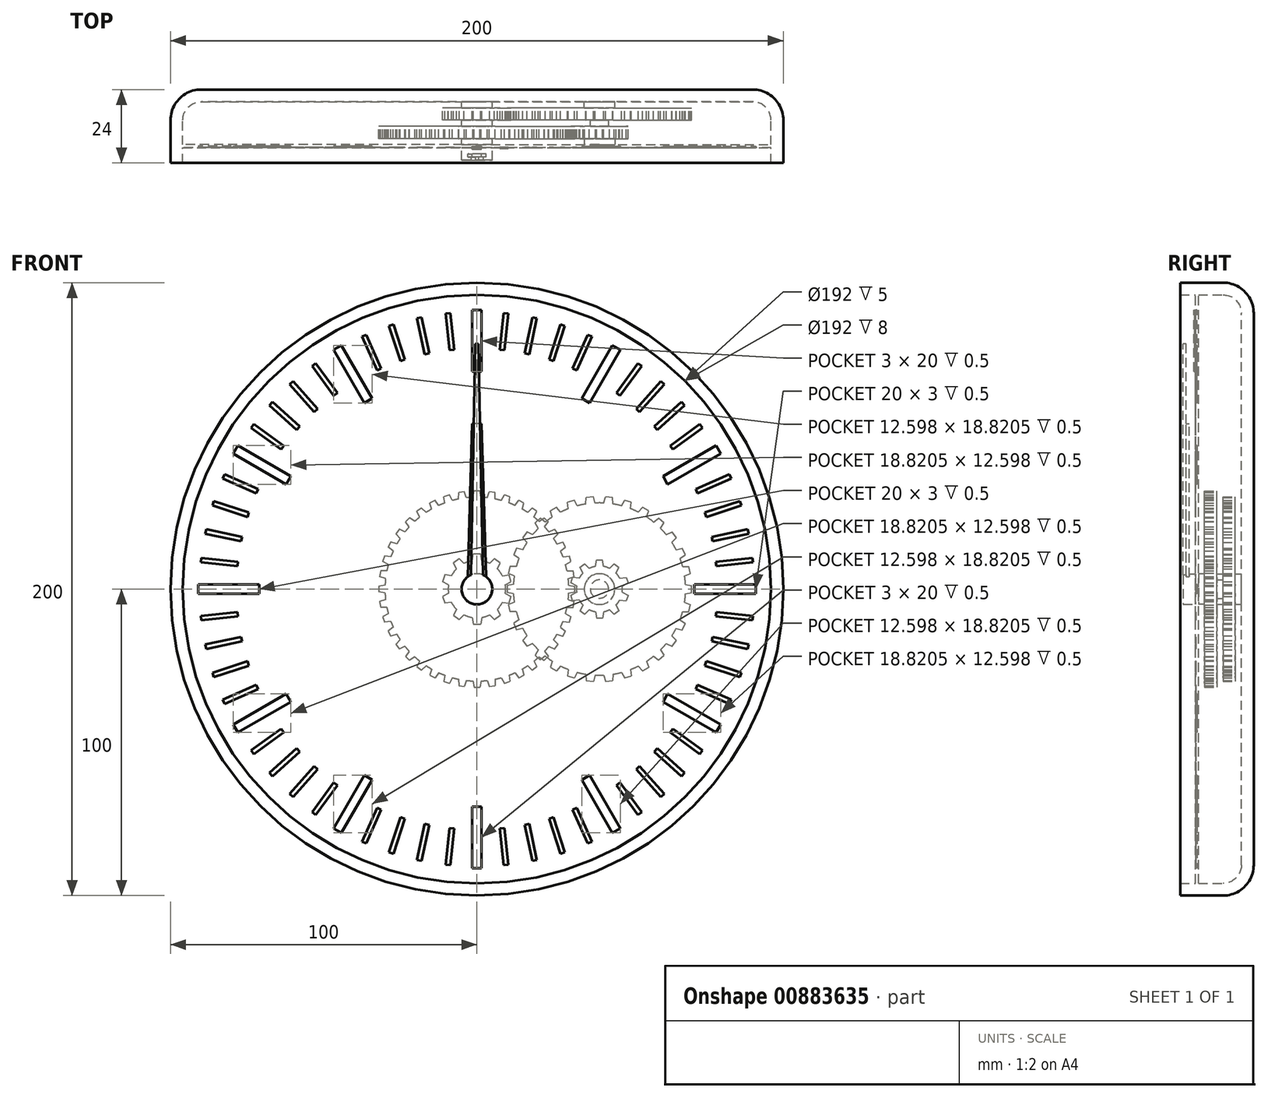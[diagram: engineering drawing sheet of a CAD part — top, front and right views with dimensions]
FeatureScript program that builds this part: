
annotation { "Feature Type Name" : "Feature", "Feature Type Description" : "" }
export const myFeature = defineFeature(function(context is Context, id is Id, definition is map)
    precondition{}
    {
        {
            var Q0;
            Q0=qCreatedBy(makeId("Front.planeOp"),FACE);
            var sketch = newSketch(context, id + "F0", { "sketchPlane" : qUnion([Q0])});
            skCircle(sketch, "E0", {"center": v(0, 0) * mm, "radius": 100 * mm});
            skSolve(sketch);
        }
        {
            var Q0;
            Q0 = qSketchRegion(id + "F0", true);
            extrude(context, id + "F1", {"entities" : qUnion([Q0]), "depth" : 24 * mm, "offsetDistance" : 25 * mm});
        }
        {
            var Q0;
            Q0=makeQuery(id+"F1.opExtrude","CAP_EDGE",EDGE,{"disambiguationData":[OSD([sQuery(id+"F0.wireOp",EDGE,"E0")])],"isStart":true});
            fillet(context, id + "F2", {"entities" : qUnion([Q0]), "radius" : 10 * mm, "tangentPropagation" : true, "allowEdgeOverflow" : false});
        }
        {
            var Q0;
            Q0=makeQuery(id+"F1.opExtrude","CAP_FACE",FACE,{"disambiguationData":[OSD([sQuery(id+"F0.wireOp",EDGE,"E0")])],"isStart":false});
            shell(context, id + "F3", {"entities" : qUnion([Q0]), "thickness" : 4 * mm});
        }
        {
            var Q0;
            {var subQ0=sQuery(id+"F0.wireOp",EDGE,"E0");Q0=makeQuery(id+"F3.opShell","OFFSET_FACE",FACE,{"disambiguationData":[OSD([subQ0]),TDD([makeQuery(id+"F1.opExtrude","CAP_FACE",FACE,{"disambiguationData":[OSD([subQ0])],"isStart":true})])]});}
            var sketch = newSketch(context, id + "F4", { "sketchPlane" : qUnion([Q0])});
            skCircle(sketch, "E1", {"center": v(40, 0) * mm, "radius": 3 * mm});
            skCircle(sketch, "E2", {"center": v(40, 0) * mm, "radius": 5 * mm});
            skCircle(sketch, "E3", {"center": v(0, 0) * mm, "radius": 3 * mm});
            skCircle(sketch, "E4", {"center": v(0, 0) * mm, "radius": 5 * mm});
            skSolve(sketch);
        }
        {
            var Q0;
            Q0 = qSketchRegion(id + "F4", true);
            extrude(context, id + "F5", {"entities" : qUnion([Q0]), "operationType" : NewBodyOperationType.ADD, "depth" : 2 * mm, "offsetDistance" : 25 * mm});
        }
        {
            var Q0;
            {var subQ0=sQuery(id+"F0.wireOp",EDGE,"E0");Q0=makeQuery(id+"F5.boolean.opBoolean","SPLIT",FACE,{"disambiguationData":[TD([makeQuery(id+"F5.opExtrude","SWEPT_FACE",FACE,{"disambiguationData":[OSD([sQuery(id+"F4.wireOp",EDGE,"E3")])]})])],"derivedFrom":makeQuery(id+"F3.opShell","OFFSET_FACE",FACE,{"disambiguationData":[OSD([subQ0]),TDD([makeQuery(id+"F1.opExtrude","CAP_FACE",FACE,{"disambiguationData":[OSD([subQ0])],"isStart":true})])]})});}
            extrude(context, id + "F6", {"entities" : qUnion([Q0]), "depth" : 19 * mm, "offsetDistance" : 25 * mm});
        }
        {
            var Q0;
            {var subQ0=sQuery(id+"F0.wireOp",EDGE,"E0");Q0=makeQuery(id+"F5.boolean.opBoolean","SPLIT",FACE,{"disambiguationData":[TD([makeQuery(id+"F5.opExtrude","SWEPT_FACE",FACE,{"disambiguationData":[OSD([sQuery(id+"F4.wireOp",EDGE,"E1")])]})])],"derivedFrom":makeQuery(id+"F3.opShell","OFFSET_FACE",FACE,{"disambiguationData":[OSD([subQ0]),TDD([makeQuery(id+"F1.opExtrude","CAP_FACE",FACE,{"disambiguationData":[OSD([subQ0])],"isStart":true})])]})});}
            extrude(context, id + "F7", {"entities" : qUnion([Q0]), "depth" : 8 * mm, "offsetDistance" : 25 * mm});
        }
        {
            var Q0;
            Q0=makeQuery(id+"F5.opExtrude","CAP_FACE",FACE,{"disambiguationData":[OSD([sQuery(id+"F4.wireOp",EDGE,"E3"),sQuery(id+"F4.wireOp",EDGE,"E4")])],"isStart":false});
            var sketch = newSketch(context, id + "F8", { "sketchPlane" : qUnion([Q0])});
            skCircle(sketch, "E5", {"center": v(0, 0) * mm, "radius": 9.38 * mm});
            skLineSegment(sketch, "E6", {"start": v(1.55, 9.25) * mm, "end": v(1.18, 11.38) * mm});
            skLineSegment(sketch, "E7", {"start": v(1.18, 11.38) * mm, "end": v(0, 11.38) * mm});
            skLineSegment(sketch, "E8.MirrorCS", {"start": v(-1.18, 11.38) * mm, "end": v(0, 11.38) * mm});
            skLineSegment(sketch, "E9.MirrorCS", {"start": v(-1.55, 9.25) * mm, "end": v(-1.18, 11.38) * mm});
            skLineSegment(sketch, "E10.1.0", {"start": v(-6.7, 6.57) * mm, "end": v(-7.64, 8.51) * mm});
            skLineSegment(sketch, "E10.1.1", {"start": v(-7.64, 8.51) * mm, "end": v(-6.69, 9.2) * mm});
            skLineSegment(sketch, "E10.1.2", {"start": v(-5.73, 9.9) * mm, "end": v(-6.69, 9.2) * mm});
            skLineSegment(sketch, "E10.1.3", {"start": v(-4.18, 8.4) * mm, "end": v(-5.73, 9.9) * mm});
            skLineSegment(sketch, "E10.2.0", {"start": v(-9.27, 1.38) * mm, "end": v(-11.18, 2.4) * mm});
            skLineSegment(sketch, "E10.2.1", {"start": v(-11.18, 2.4) * mm, "end": v(-10.82, 3.52) * mm});
            skLineSegment(sketch, "E10.2.2", {"start": v(-10.45, 4.64) * mm, "end": v(-10.82, 3.52) * mm});
            skLineSegment(sketch, "E10.2.3", {"start": v(-8.31, 4.33) * mm, "end": v(-10.45, 4.64) * mm});
            skLineSegment(sketch, "E11.1.3.0", {"start": v(-8.31, -4.33) * mm, "end": v(-10.45, -4.64) * mm});
            skLineSegment(sketch, "E11.3.3.0", {"start": v(-10.45, -4.64) * mm, "end": v(-10.82, -3.52) * mm});
            skLineSegment(sketch, "E11.6.3.0", {"start": v(-11.18, -2.4) * mm, "end": v(-10.82, -3.52) * mm});
            skLineSegment(sketch, "E11.9.3.0", {"start": v(-9.27, -1.38) * mm, "end": v(-11.18, -2.4) * mm});
            skLineSegment(sketch, "E11.1.4.0", {"start": v(-4.18, -8.4) * mm, "end": v(-5.73, -9.9) * mm});
            skLineSegment(sketch, "E11.3.4.0", {"start": v(-5.73, -9.9) * mm, "end": v(-6.69, -9.2) * mm});
            skLineSegment(sketch, "E11.6.4.0", {"start": v(-7.64, -8.51) * mm, "end": v(-6.69, -9.2) * mm});
            skLineSegment(sketch, "E11.9.4.0", {"start": v(-6.7, -6.57) * mm, "end": v(-7.64, -8.51) * mm});
            skLineSegment(sketch, "E11.1.5.0", {"start": v(1.55, -9.25) * mm, "end": v(1.18, -11.38) * mm});
            skLineSegment(sketch, "E11.3.5.0", {"start": v(1.18, -11.38) * mm, "end": v(0, -11.38) * mm});
            skLineSegment(sketch, "E11.6.5.0", {"start": v(-1.18, -11.38) * mm, "end": v(0, -11.38) * mm});
            skLineSegment(sketch, "E11.9.5.0", {"start": v(-1.55, -9.25) * mm, "end": v(-1.18, -11.38) * mm});
            skLineSegment(sketch, "E11.1.6.0", {"start": v(6.7, -6.57) * mm, "end": v(7.64, -8.51) * mm});
            skLineSegment(sketch, "E11.3.6.0", {"start": v(7.64, -8.51) * mm, "end": v(6.69, -9.2) * mm});
            skLineSegment(sketch, "E11.6.6.0", {"start": v(5.73, -9.9) * mm, "end": v(6.69, -9.2) * mm});
            skLineSegment(sketch, "E11.9.6.0", {"start": v(4.18, -8.4) * mm, "end": v(5.73, -9.9) * mm});
            skLineSegment(sketch, "E11.1.7.0", {"start": v(9.27, -1.38) * mm, "end": v(11.18, -2.4) * mm});
            skLineSegment(sketch, "E11.3.7.0", {"start": v(11.18, -2.4) * mm, "end": v(10.82, -3.52) * mm});
            skLineSegment(sketch, "E11.6.7.0", {"start": v(10.45, -4.64) * mm, "end": v(10.82, -3.52) * mm});
            skLineSegment(sketch, "E11.9.7.0", {"start": v(8.31, -4.33) * mm, "end": v(10.45, -4.64) * mm});
            skLineSegment(sketch, "E11.1.8.0", {"start": v(8.31, 4.33) * mm, "end": v(10.45, 4.64) * mm});
            skLineSegment(sketch, "E11.3.8.0", {"start": v(10.45, 4.64) * mm, "end": v(10.82, 3.52) * mm});
            skLineSegment(sketch, "E11.6.8.0", {"start": v(11.18, 2.4) * mm, "end": v(10.82, 3.52) * mm});
            skLineSegment(sketch, "E11.9.8.0", {"start": v(9.27, 1.38) * mm, "end": v(11.18, 2.4) * mm});
            skLineSegment(sketch, "E11.1.9.0", {"start": v(4.18, 8.4) * mm, "end": v(5.73, 9.9) * mm});
            skLineSegment(sketch, "E11.3.9.0", {"start": v(5.73, 9.9) * mm, "end": v(6.69, 9.2) * mm});
            skLineSegment(sketch, "E11.6.9.0", {"start": v(7.64, 8.51) * mm, "end": v(6.69, 9.2) * mm});
            skLineSegment(sketch, "E11.9.9.0", {"start": v(6.7, 6.57) * mm, "end": v(7.64, 8.51) * mm});
            skSolve(sketch);
        }
        {
            var Q0;
            Q0 = qSketchRegion(id + "F8", true);
            extrude(context, id + "F9", {"entities" : qUnion([Q0]), "operationType" : NewBodyOperationType.ADD, "depth" : 4 * mm, "offsetDistance" : 25 * mm});
        }
        {
            var Q0;
            Q0=makeQuery(id+"F5.opExtrude","CAP_FACE",FACE,{"disambiguationData":[OSD([sQuery(id+"F4.wireOp",EDGE,"E1"),sQuery(id+"F4.wireOp",EDGE,"E2")])],"isStart":false});
            var sketch = newSketch(context, id + "F10", { "sketchPlane" : qUnion([Q0])});
            skCircle(sketch, "E12", {"center": v(40, 0) * mm, "radius": 28.12 * mm});
            skLineSegment(sketch, "E13", {"start": v(11.92, 1.54) * mm, "end": v(9.88, 1.18) * mm});
            skLineSegment(sketch, "E14", {"start": v(9.88, 1.18) * mm, "end": v(9.88, 0) * mm});
            skLineSegment(sketch, "E15.MirrorCS", {"start": v(11.92, -1.54) * mm, "end": v(9.88, -1.18) * mm});
            skLineSegment(sketch, "E16.MirrorCS", {"start": v(9.88, -1.18) * mm, "end": v(9.88, 0) * mm});
            skLineSegment(sketch, "E17.1.0", {"start": v(12.21, -4.33) * mm, "end": v(10.29, -5.11) * mm});
            skLineSegment(sketch, "E17.1.1", {"start": v(10.29, -5.11) * mm, "end": v(10.53, -6.26) * mm});
            skLineSegment(sketch, "E17.1.2", {"start": v(10.78, -7.42) * mm, "end": v(10.53, -6.26) * mm});
            skLineSegment(sketch, "E17.1.3", {"start": v(12.85, -7.34) * mm, "end": v(10.78, -7.42) * mm});
            skLineSegment(sketch, "E17.2.0", {"start": v(13.72, -10.02) * mm, "end": v(12, -11.18) * mm});
            skLineSegment(sketch, "E17.2.1", {"start": v(12, -11.18) * mm, "end": v(12.48, -12.25) * mm});
            skLineSegment(sketch, "E17.2.2", {"start": v(12.96, -13.33) * mm, "end": v(12.48, -12.25) * mm});
            skLineSegment(sketch, "E17.2.3", {"start": v(14.97, -12.83) * mm, "end": v(12.96, -13.33) * mm});
            skLineSegment(sketch, "E18.2.3.0", {"start": v(16.38, -15.26) * mm, "end": v(14.94, -16.75) * mm});
            skLineSegment(sketch, "E18.3.3.0", {"start": v(14.94, -16.75) * mm, "end": v(15.63, -17.7) * mm});
            skLineSegment(sketch, "E18.6.3.0", {"start": v(16.32, -18.66) * mm, "end": v(15.63, -17.7) * mm});
            skLineSegment(sketch, "E18.9.3.0", {"start": v(18.18, -17.75) * mm, "end": v(16.32, -18.66) * mm});
            skLineSegment(sketch, "E18.2.4.0", {"start": v(20.07, -19.84) * mm, "end": v(18.97, -21.6) * mm});
            skLineSegment(sketch, "E18.3.4.0", {"start": v(18.97, -21.6) * mm, "end": v(19.84, -22.39) * mm});
            skLineSegment(sketch, "E18.6.4.0", {"start": v(20.72, -23.18) * mm, "end": v(19.84, -22.39) * mm});
            skLineSegment(sketch, "E18.9.4.0", {"start": v(22.35, -21.9) * mm, "end": v(20.72, -23.18) * mm});
            skLineSegment(sketch, "E18.2.5.0", {"start": v(24.63, -23.55) * mm, "end": v(23.92, -25.5) * mm});
            skLineSegment(sketch, "E18.3.5.0", {"start": v(23.92, -25.5) * mm, "end": v(24.94, -26.09) * mm});
            skLineSegment(sketch, "E18.6.5.0", {"start": v(25.96, -26.68) * mm, "end": v(24.94, -26.09) * mm});
            skLineSegment(sketch, "E18.9.5.0", {"start": v(27.3, -25.09) * mm, "end": v(25.96, -26.68) * mm});
            skLineSegment(sketch, "E18.2.6.0", {"start": v(29.86, -26.23) * mm, "end": v(29.57, -28.29) * mm});
            skLineSegment(sketch, "E18.3.6.0", {"start": v(29.57, -28.29) * mm, "end": v(30.7, -28.65) * mm});
            skLineSegment(sketch, "E18.6.6.0", {"start": v(31.81, -29.01) * mm, "end": v(30.7, -28.65) * mm});
            skLineSegment(sketch, "E18.9.6.0", {"start": v(32.78, -27.18) * mm, "end": v(31.81, -29.01) * mm});
            skLineSegment(sketch, "E18.2.7.0", {"start": v(35.53, -27.77) * mm, "end": v(35.68, -29.84) * mm});
            skLineSegment(sketch, "E18.3.7.0", {"start": v(35.68, -29.84) * mm, "end": v(36.85, -29.96) * mm});
            skLineSegment(sketch, "E18.6.7.0", {"start": v(38.02, -30.08) * mm, "end": v(36.85, -29.96) * mm});
            skLineSegment(sketch, "E18.9.7.0", {"start": v(38.6, -28.09) * mm, "end": v(38.02, -30.08) * mm});
            skLineSegment(sketch, "E18.2.8.0", {"start": v(41.4, -28.09) * mm, "end": v(41.98, -30.08) * mm});
            skLineSegment(sketch, "E18.3.8.0", {"start": v(41.98, -30.08) * mm, "end": v(43.15, -29.96) * mm});
            skLineSegment(sketch, "E18.6.8.0", {"start": v(44.32, -29.84) * mm, "end": v(43.15, -29.96) * mm});
            skLineSegment(sketch, "E18.9.8.0", {"start": v(44.47, -27.77) * mm, "end": v(44.32, -29.84) * mm});
            skLineSegment(sketch, "E18.2.9.0", {"start": v(47.22, -27.18) * mm, "end": v(48.19, -29.01) * mm});
            skLineSegment(sketch, "E18.3.9.0", {"start": v(48.19, -29.01) * mm, "end": v(49.3, -28.65) * mm});
            skLineSegment(sketch, "E18.6.9.0", {"start": v(50.43, -28.29) * mm, "end": v(49.3, -28.65) * mm});
            skLineSegment(sketch, "E18.9.9.0", {"start": v(50.14, -26.23) * mm, "end": v(50.43, -28.29) * mm});
            skLineSegment(sketch, "E18.2.10.0", {"start": v(52.7, -25.09) * mm, "end": v(54.04, -26.68) * mm});
            skLineSegment(sketch, "E18.3.10.0", {"start": v(54.04, -26.68) * mm, "end": v(55.06, -26.09) * mm});
            skLineSegment(sketch, "E18.6.10.0", {"start": v(56.08, -25.5) * mm, "end": v(55.06, -26.09) * mm});
            skLineSegment(sketch, "E18.9.10.0", {"start": v(55.37, -23.55) * mm, "end": v(56.08, -25.5) * mm});
            skLineSegment(sketch, "E18.2.11.0", {"start": v(57.65, -21.9) * mm, "end": v(59.28, -23.18) * mm});
            skLineSegment(sketch, "E18.3.11.0", {"start": v(59.28, -23.18) * mm, "end": v(60.16, -22.39) * mm});
            skLineSegment(sketch, "E18.6.11.0", {"start": v(61.03, -21.6) * mm, "end": v(60.16, -22.39) * mm});
            skLineSegment(sketch, "E18.9.11.0", {"start": v(59.93, -19.84) * mm, "end": v(61.03, -21.6) * mm});
            skLineSegment(sketch, "E18.2.12.0", {"start": v(61.82, -17.75) * mm, "end": v(63.68, -18.66) * mm});
            skLineSegment(sketch, "E18.3.12.0", {"start": v(63.68, -18.66) * mm, "end": v(64.37, -17.7) * mm});
            skLineSegment(sketch, "E18.6.12.0", {"start": v(65.06, -16.75) * mm, "end": v(64.37, -17.7) * mm});
            skLineSegment(sketch, "E18.9.12.0", {"start": v(63.62, -15.26) * mm, "end": v(65.06, -16.75) * mm});
            skLineSegment(sketch, "E18.2.13.0", {"start": v(65.03, -12.83) * mm, "end": v(67.04, -13.33) * mm});
            skLineSegment(sketch, "E18.3.13.0", {"start": v(67.04, -13.33) * mm, "end": v(67.52, -12.25) * mm});
            skLineSegment(sketch, "E18.6.13.0", {"start": v(68, -11.18) * mm, "end": v(67.52, -12.25) * mm});
            skLineSegment(sketch, "E18.9.13.0", {"start": v(66.28, -10.02) * mm, "end": v(68, -11.18) * mm});
            skLineSegment(sketch, "E18.2.14.0", {"start": v(67.15, -7.34) * mm, "end": v(69.22, -7.42) * mm});
            skLineSegment(sketch, "E18.3.14.0", {"start": v(69.22, -7.42) * mm, "end": v(69.47, -6.26) * mm});
            skLineSegment(sketch, "E18.6.14.0", {"start": v(69.71, -5.11) * mm, "end": v(69.47, -6.26) * mm});
            skLineSegment(sketch, "E18.9.14.0", {"start": v(67.79, -4.33) * mm, "end": v(69.71, -5.11) * mm});
            skLineSegment(sketch, "E18.2.15.0", {"start": v(68.08, -1.54) * mm, "end": v(70.12, -1.18) * mm});
            skLineSegment(sketch, "E18.3.15.0", {"start": v(70.12, -1.18) * mm, "end": v(70.12, 0) * mm});
            skLineSegment(sketch, "E18.6.15.0", {"start": v(70.12, 1.18) * mm, "end": v(70.12, 0) * mm});
            skLineSegment(sketch, "E18.9.15.0", {"start": v(68.08, 1.54) * mm, "end": v(70.12, 1.18) * mm});
            skLineSegment(sketch, "E18.2.16.0", {"start": v(67.79, 4.33) * mm, "end": v(69.71, 5.11) * mm});
            skLineSegment(sketch, "E18.3.16.0", {"start": v(69.71, 5.11) * mm, "end": v(69.47, 6.26) * mm});
            skLineSegment(sketch, "E18.6.16.0", {"start": v(69.22, 7.42) * mm, "end": v(69.47, 6.26) * mm});
            skLineSegment(sketch, "E18.9.16.0", {"start": v(67.15, 7.34) * mm, "end": v(69.22, 7.42) * mm});
            skLineSegment(sketch, "E18.2.17.0", {"start": v(66.28, 10.02) * mm, "end": v(68, 11.18) * mm});
            skLineSegment(sketch, "E18.3.17.0", {"start": v(68, 11.18) * mm, "end": v(67.52, 12.25) * mm});
            skLineSegment(sketch, "E18.6.17.0", {"start": v(67.04, 13.33) * mm, "end": v(67.52, 12.25) * mm});
            skLineSegment(sketch, "E18.9.17.0", {"start": v(65.03, 12.83) * mm, "end": v(67.04, 13.33) * mm});
            skLineSegment(sketch, "E18.2.18.0", {"start": v(63.62, 15.26) * mm, "end": v(65.06, 16.75) * mm});
            skLineSegment(sketch, "E18.3.18.0", {"start": v(65.06, 16.75) * mm, "end": v(64.37, 17.7) * mm});
            skLineSegment(sketch, "E18.6.18.0", {"start": v(63.68, 18.66) * mm, "end": v(64.37, 17.7) * mm});
            skLineSegment(sketch, "E18.9.18.0", {"start": v(61.82, 17.75) * mm, "end": v(63.68, 18.66) * mm});
            skLineSegment(sketch, "E18.2.19.0", {"start": v(59.93, 19.84) * mm, "end": v(61.03, 21.6) * mm});
            skLineSegment(sketch, "E18.3.19.0", {"start": v(61.03, 21.6) * mm, "end": v(60.16, 22.39) * mm});
            skLineSegment(sketch, "E18.6.19.0", {"start": v(59.28, 23.18) * mm, "end": v(60.16, 22.39) * mm});
            skLineSegment(sketch, "E18.9.19.0", {"start": v(57.65, 21.9) * mm, "end": v(59.28, 23.18) * mm});
            skLineSegment(sketch, "E18.2.20.0", {"start": v(55.37, 23.55) * mm, "end": v(56.08, 25.5) * mm});
            skLineSegment(sketch, "E18.3.20.0", {"start": v(56.08, 25.5) * mm, "end": v(55.06, 26.09) * mm});
            skLineSegment(sketch, "E18.6.20.0", {"start": v(54.04, 26.68) * mm, "end": v(55.06, 26.09) * mm});
            skLineSegment(sketch, "E18.9.20.0", {"start": v(52.7, 25.09) * mm, "end": v(54.04, 26.68) * mm});
            skLineSegment(sketch, "E18.2.21.0", {"start": v(50.14, 26.23) * mm, "end": v(50.43, 28.29) * mm});
            skLineSegment(sketch, "E18.3.21.0", {"start": v(50.43, 28.29) * mm, "end": v(49.3, 28.65) * mm});
            skLineSegment(sketch, "E18.6.21.0", {"start": v(48.19, 29.01) * mm, "end": v(49.3, 28.65) * mm});
            skLineSegment(sketch, "E18.9.21.0", {"start": v(47.22, 27.18) * mm, "end": v(48.19, 29.01) * mm});
            skLineSegment(sketch, "E18.2.22.0", {"start": v(44.47, 27.77) * mm, "end": v(44.32, 29.84) * mm});
            skLineSegment(sketch, "E18.3.22.0", {"start": v(44.32, 29.84) * mm, "end": v(43.15, 29.96) * mm});
            skLineSegment(sketch, "E18.6.22.0", {"start": v(41.98, 30.08) * mm, "end": v(43.15, 29.96) * mm});
            skLineSegment(sketch, "E18.9.22.0", {"start": v(41.4, 28.09) * mm, "end": v(41.98, 30.08) * mm});
            skLineSegment(sketch, "E18.2.23.0", {"start": v(38.6, 28.09) * mm, "end": v(38.02, 30.08) * mm});
            skLineSegment(sketch, "E18.3.23.0", {"start": v(38.02, 30.08) * mm, "end": v(36.85, 29.96) * mm});
            skLineSegment(sketch, "E18.6.23.0", {"start": v(35.68, 29.84) * mm, "end": v(36.85, 29.96) * mm});
            skLineSegment(sketch, "E18.9.23.0", {"start": v(35.53, 27.77) * mm, "end": v(35.68, 29.84) * mm});
            skLineSegment(sketch, "E18.2.24.0", {"start": v(32.78, 27.18) * mm, "end": v(31.81, 29.01) * mm});
            skLineSegment(sketch, "E18.3.24.0", {"start": v(31.81, 29.01) * mm, "end": v(30.7, 28.65) * mm});
            skLineSegment(sketch, "E18.6.24.0", {"start": v(29.57, 28.29) * mm, "end": v(30.7, 28.65) * mm});
            skLineSegment(sketch, "E18.9.24.0", {"start": v(29.86, 26.23) * mm, "end": v(29.57, 28.29) * mm});
            skLineSegment(sketch, "E18.2.25.0", {"start": v(27.3, 25.09) * mm, "end": v(25.96, 26.68) * mm});
            skLineSegment(sketch, "E18.3.25.0", {"start": v(25.96, 26.68) * mm, "end": v(24.94, 26.09) * mm});
            skLineSegment(sketch, "E18.6.25.0", {"start": v(23.92, 25.5) * mm, "end": v(24.94, 26.09) * mm});
            skLineSegment(sketch, "E18.9.25.0", {"start": v(24.63, 23.55) * mm, "end": v(23.92, 25.5) * mm});
            skLineSegment(sketch, "E18.2.26.0", {"start": v(22.35, 21.9) * mm, "end": v(20.72, 23.18) * mm});
            skLineSegment(sketch, "E18.3.26.0", {"start": v(20.72, 23.18) * mm, "end": v(19.84, 22.39) * mm});
            skLineSegment(sketch, "E18.6.26.0", {"start": v(18.97, 21.6) * mm, "end": v(19.84, 22.39) * mm});
            skLineSegment(sketch, "E18.9.26.0", {"start": v(20.07, 19.84) * mm, "end": v(18.97, 21.6) * mm});
            skLineSegment(sketch, "E18.2.27.0", {"start": v(18.18, 17.75) * mm, "end": v(16.32, 18.66) * mm});
            skLineSegment(sketch, "E18.3.27.0", {"start": v(16.32, 18.66) * mm, "end": v(15.63, 17.7) * mm});
            skLineSegment(sketch, "E18.6.27.0", {"start": v(14.94, 16.75) * mm, "end": v(15.63, 17.7) * mm});
            skLineSegment(sketch, "E18.9.27.0", {"start": v(16.38, 15.26) * mm, "end": v(14.94, 16.75) * mm});
            skLineSegment(sketch, "E18.2.28.0", {"start": v(14.97, 12.83) * mm, "end": v(12.96, 13.33) * mm});
            skLineSegment(sketch, "E18.3.28.0", {"start": v(12.96, 13.33) * mm, "end": v(12.48, 12.25) * mm});
            skLineSegment(sketch, "E18.6.28.0", {"start": v(12, 11.18) * mm, "end": v(12.48, 12.25) * mm});
            skLineSegment(sketch, "E18.9.28.0", {"start": v(13.72, 10.02) * mm, "end": v(12, 11.18) * mm});
            skLineSegment(sketch, "E18.2.29.0", {"start": v(12.85, 7.34) * mm, "end": v(10.78, 7.42) * mm});
            skLineSegment(sketch, "E18.3.29.0", {"start": v(10.78, 7.42) * mm, "end": v(10.53, 6.26) * mm});
            skLineSegment(sketch, "E18.6.29.0", {"start": v(10.29, 5.11) * mm, "end": v(10.53, 6.26) * mm});
            skLineSegment(sketch, "E18.9.29.0", {"start": v(12.21, 4.33) * mm, "end": v(10.29, 5.11) * mm});
            skSolve(sketch);
        }
        {
            var Q0;
            Q0 = qSketchRegion(id + "F10", true);
            extrude(context, id + "F11", {"entities" : qUnion([Q0]), "operationType" : NewBodyOperationType.ADD, "depth" : 4 * mm, "offsetDistance" : 25 * mm});
        }
        {
            var Q0;
            Q0=makeQuery(id+"F9.opExtrude","CAP_FACE",FACE,{"disambiguationData":[OSD([sQuery(id+"F8.wireOp",EDGE,"E5"),sQuery(id+"F8.wireOp",EDGE,"E6"),sQuery(id+"F8.wireOp",EDGE,"E7"),sQuery(id+"F8.wireOp",EDGE,"E8.MirrorCS"),sQuery(id+"F8.wireOp",EDGE,"E9.MirrorCS"),sQuery(id+"F8.wireOp",EDGE,"E10.1.0"),sQuery(id+"F8.wireOp",EDGE,"E10.1.1"),sQuery(id+"F8.wireOp",EDGE,"E10.1.2"),sQuery(id+"F8.wireOp",EDGE,"E10.1.3"),sQuery(id+"F8.wireOp",EDGE,"E10.2.0"),sQuery(id+"F8.wireOp",EDGE,"E10.2.1"),sQuery(id+"F8.wireOp",EDGE,"E10.2.2"),sQuery(id+"F8.wireOp",EDGE,"E10.2.3"),sQuery(id+"F8.wireOp",EDGE,"E11.1.3.0"),sQuery(id+"F8.wireOp",EDGE,"E11.3.3.0"),sQuery(id+"F8.wireOp",EDGE,"E11.6.3.0"),sQuery(id+"F8.wireOp",EDGE,"E11.9.3.0"),sQuery(id+"F8.wireOp",EDGE,"E11.1.4.0"),sQuery(id+"F8.wireOp",EDGE,"E11.3.4.0"),sQuery(id+"F8.wireOp",EDGE,"E11.6.4.0"),sQuery(id+"F8.wireOp",EDGE,"E11.9.4.0"),sQuery(id+"F8.wireOp",EDGE,"E11.1.5.0"),sQuery(id+"F8.wireOp",EDGE,"E11.3.5.0"),sQuery(id+"F8.wireOp",EDGE,"E11.6.5.0"),sQuery(id+"F8.wireOp",EDGE,"E11.9.5.0"),sQuery(id+"F8.wireOp",EDGE,"E11.1.6.0"),sQuery(id+"F8.wireOp",EDGE,"E11.3.6.0"),sQuery(id+"F8.wireOp",EDGE,"E11.6.6.0"),sQuery(id+"F8.wireOp",EDGE,"E11.9.6.0"),sQuery(id+"F8.wireOp",EDGE,"E11.1.7.0"),sQuery(id+"F8.wireOp",EDGE,"E11.3.7.0"),sQuery(id+"F8.wireOp",EDGE,"E11.6.7.0"),sQuery(id+"F8.wireOp",EDGE,"E11.9.7.0"),sQuery(id+"F8.wireOp",EDGE,"E11.1.8.0"),sQuery(id+"F8.wireOp",EDGE,"E11.3.8.0"),sQuery(id+"F8.wireOp",EDGE,"E11.6.8.0"),sQuery(id+"F8.wireOp",EDGE,"E11.9.8.0"),sQuery(id+"F8.wireOp",EDGE,"E11.1.9.0"),sQuery(id+"F8.wireOp",EDGE,"E11.3.9.0"),sQuery(id+"F8.wireOp",EDGE,"E11.6.9.0"),sQuery(id+"F8.wireOp",EDGE,"E11.9.9.0")])],"isStart":false});
            var sketch = newSketch(context, id + "F12", { "sketchPlane" : qUnion([Q0])});
            skCircle(sketch, "E19.0", {"center": v(0, 0) * mm, "radius": 3 * mm});
            skCircle(sketch, "E20.0", {"center": v(0, 0) * mm, "radius": 5 * mm});
            skSolve(sketch);
        }
        {
            var Q0;
            Q0 = qSketchRegion(id + "F12", true);
            extrude(context, id + "F13", {"entities" : qUnion([Q0]), "depth" : 2 * mm, "offsetDistance" : 25 * mm});
        }
        {
            var Q0;
            Q0=makeQuery(id+"F13.opExtrude","CAP_FACE",FACE,{"disambiguationData":[OSD([sQuery(id+"F12.wireOp",EDGE,"E19.0"),sQuery(id+"F12.wireOp",EDGE,"E20.0")])],"isStart":false});
            var sketch = newSketch(context, id + "F14", { "sketchPlane" : qUnion([Q0])});
            skCircle(sketch, "E21.0", {"center": v(0, 0) * mm, "radius": 3 * mm});
            skCircle(sketch, "E22", {"center": v(0, 0) * mm, "radius": 30 * mm});
            skLineSegment(sketch, "E23", {"start": v(1.3, 29.97) * mm, "end": v(0.94, 32) * mm});
            skLineSegment(sketch, "E24", {"start": v(0.94, 32) * mm, "end": v(0, 32) * mm});
            skLineSegment(sketch, "E25.MirrorCS", {"start": v(-0.94, 32) * mm, "end": v(0, 32) * mm});
            skLineSegment(sketch, "E26.MirrorCS", {"start": v(-1.3, 29.97) * mm, "end": v(-0.94, 32) * mm});
            skLineSegment(sketch, "E27.1.0", {"start": v(-3.4, 29.8) * mm, "end": v(-4.08, 31.75) * mm});
            skLineSegment(sketch, "E27.1.1", {"start": v(-4.08, 31.75) * mm, "end": v(-5, 31.6) * mm});
            skLineSegment(sketch, "E27.1.2", {"start": v(-5.94, 31.46) * mm, "end": v(-5, 31.6) * mm});
            skLineSegment(sketch, "E27.1.3", {"start": v(-5.97, 29.4) * mm, "end": v(-5.94, 31.46) * mm});
            skLineSegment(sketch, "E27.2.0", {"start": v(-8.03, 28.9) * mm, "end": v(-9, 30.73) * mm});
            skLineSegment(sketch, "E27.2.1", {"start": v(-9, 30.73) * mm, "end": v(-9.89, 30.43) * mm});
            skLineSegment(sketch, "E27.2.2", {"start": v(-10.78, 30.14) * mm, "end": v(-9.89, 30.43) * mm});
            skLineSegment(sketch, "E27.2.3", {"start": v(-10.5, 28.1) * mm, "end": v(-10.78, 30.14) * mm});
            skLineSegment(sketch, "E28.1.3.0", {"start": v(-12.45, 27.3) * mm, "end": v(-13.69, 28.94) * mm});
            skLineSegment(sketch, "E28.3.3.0", {"start": v(-13.69, 28.94) * mm, "end": v(-14.53, 28.51) * mm});
            skLineSegment(sketch, "E28.6.3.0", {"start": v(-15.37, 28.08) * mm, "end": v(-14.53, 28.51) * mm});
            skLineSegment(sketch, "E28.9.3.0", {"start": v(-14.77, 26.11) * mm, "end": v(-15.37, 28.08) * mm});
            skLineSegment(sketch, "E28.1.4.0", {"start": v(-16.57, 25.01) * mm, "end": v(-18.05, 26.44) * mm});
            skLineSegment(sketch, "E28.3.4.0", {"start": v(-18.05, 26.44) * mm, "end": v(-18.8, 25.89) * mm});
            skLineSegment(sketch, "E28.6.4.0", {"start": v(-19.57, 25.33) * mm, "end": v(-18.8, 25.89) * mm});
            skLineSegment(sketch, "E28.9.4.0", {"start": v(-18.67, 23.48) * mm, "end": v(-19.57, 25.33) * mm});
            skLineSegment(sketch, "E28.1.5.0", {"start": v(-20.27, 22.11) * mm, "end": v(-21.96, 23.3) * mm});
            skLineSegment(sketch, "E28.3.5.0", {"start": v(-21.96, 23.3) * mm, "end": v(-22.63, 22.63) * mm});
            skLineSegment(sketch, "E28.6.5.0", {"start": v(-23.3, 21.96) * mm, "end": v(-22.63, 22.63) * mm});
            skLineSegment(sketch, "E28.9.5.0", {"start": v(-22.11, 20.27) * mm, "end": v(-23.3, 21.96) * mm});
            skLineSegment(sketch, "E28.1.6.0", {"start": v(-23.48, 18.67) * mm, "end": v(-25.33, 19.57) * mm});
            skLineSegment(sketch, "E28.3.6.0", {"start": v(-25.33, 19.57) * mm, "end": v(-25.89, 18.8) * mm});
            skLineSegment(sketch, "E28.6.6.0", {"start": v(-26.44, 18.05) * mm, "end": v(-25.89, 18.8) * mm});
            skLineSegment(sketch, "E28.9.6.0", {"start": v(-25.01, 16.57) * mm, "end": v(-26.44, 18.05) * mm});
            skLineSegment(sketch, "E28.1.7.0", {"start": v(-26.11, 14.77) * mm, "end": v(-28.08, 15.37) * mm});
            skLineSegment(sketch, "E28.3.7.0", {"start": v(-28.08, 15.37) * mm, "end": v(-28.51, 14.53) * mm});
            skLineSegment(sketch, "E28.6.7.0", {"start": v(-28.94, 13.69) * mm, "end": v(-28.51, 14.53) * mm});
            skLineSegment(sketch, "E28.9.7.0", {"start": v(-27.3, 12.45) * mm, "end": v(-28.94, 13.69) * mm});
            skLineSegment(sketch, "E28.1.8.0", {"start": v(-28.1, 10.5) * mm, "end": v(-30.14, 10.78) * mm});
            skLineSegment(sketch, "E28.3.8.0", {"start": v(-30.14, 10.78) * mm, "end": v(-30.43, 9.89) * mm});
            skLineSegment(sketch, "E28.6.8.0", {"start": v(-30.73, 9) * mm, "end": v(-30.43, 9.89) * mm});
            skLineSegment(sketch, "E28.9.8.0", {"start": v(-28.9, 8.03) * mm, "end": v(-30.73, 9) * mm});
            skLineSegment(sketch, "E28.1.9.0", {"start": v(-29.4, 5.97) * mm, "end": v(-31.46, 5.94) * mm});
            skLineSegment(sketch, "E28.3.9.0", {"start": v(-31.46, 5.94) * mm, "end": v(-31.6, 5) * mm});
            skLineSegment(sketch, "E28.6.9.0", {"start": v(-31.75, 4.08) * mm, "end": v(-31.6, 5) * mm});
            skLineSegment(sketch, "E28.9.9.0", {"start": v(-29.8, 3.4) * mm, "end": v(-31.75, 4.08) * mm});
            skLineSegment(sketch, "E28.1.10.0", {"start": v(-29.97, 1.3) * mm, "end": v(-32, 0.94) * mm});
            skLineSegment(sketch, "E28.3.10.0", {"start": v(-32, 0.94) * mm, "end": v(-32, 0) * mm});
            skLineSegment(sketch, "E28.6.10.0", {"start": v(-32, -0.94) * mm, "end": v(-32, 0) * mm});
            skLineSegment(sketch, "E28.9.10.0", {"start": v(-29.97, -1.3) * mm, "end": v(-32, -0.94) * mm});
            skLineSegment(sketch, "E28.1.11.0", {"start": v(-29.8, -3.4) * mm, "end": v(-31.75, -4.08) * mm});
            skLineSegment(sketch, "E28.3.11.0", {"start": v(-31.75, -4.08) * mm, "end": v(-31.6, -5) * mm});
            skLineSegment(sketch, "E28.6.11.0", {"start": v(-31.46, -5.94) * mm, "end": v(-31.6, -5) * mm});
            skLineSegment(sketch, "E28.9.11.0", {"start": v(-29.4, -5.97) * mm, "end": v(-31.46, -5.94) * mm});
            skLineSegment(sketch, "E28.1.12.0", {"start": v(-28.9, -8.03) * mm, "end": v(-30.73, -9) * mm});
            skLineSegment(sketch, "E28.3.12.0", {"start": v(-30.73, -9) * mm, "end": v(-30.43, -9.89) * mm});
            skLineSegment(sketch, "E28.6.12.0", {"start": v(-30.14, -10.78) * mm, "end": v(-30.43, -9.89) * mm});
            skLineSegment(sketch, "E28.9.12.0", {"start": v(-28.1, -10.5) * mm, "end": v(-30.14, -10.78) * mm});
            skLineSegment(sketch, "E28.1.13.0", {"start": v(-27.3, -12.45) * mm, "end": v(-28.94, -13.69) * mm});
            skLineSegment(sketch, "E28.3.13.0", {"start": v(-28.94, -13.69) * mm, "end": v(-28.51, -14.53) * mm});
            skLineSegment(sketch, "E28.6.13.0", {"start": v(-28.08, -15.37) * mm, "end": v(-28.51, -14.53) * mm});
            skLineSegment(sketch, "E28.9.13.0", {"start": v(-26.11, -14.77) * mm, "end": v(-28.08, -15.37) * mm});
            skLineSegment(sketch, "E28.1.14.0", {"start": v(-25.01, -16.57) * mm, "end": v(-26.44, -18.05) * mm});
            skLineSegment(sketch, "E28.3.14.0", {"start": v(-26.44, -18.05) * mm, "end": v(-25.89, -18.8) * mm});
            skLineSegment(sketch, "E28.6.14.0", {"start": v(-25.33, -19.57) * mm, "end": v(-25.89, -18.8) * mm});
            skLineSegment(sketch, "E28.9.14.0", {"start": v(-23.48, -18.67) * mm, "end": v(-25.33, -19.57) * mm});
            skLineSegment(sketch, "E28.1.15.0", {"start": v(-22.11, -20.27) * mm, "end": v(-23.3, -21.96) * mm});
            skLineSegment(sketch, "E28.3.15.0", {"start": v(-23.3, -21.96) * mm, "end": v(-22.63, -22.63) * mm});
            skLineSegment(sketch, "E28.6.15.0", {"start": v(-21.96, -23.3) * mm, "end": v(-22.63, -22.63) * mm});
            skLineSegment(sketch, "E28.9.15.0", {"start": v(-20.27, -22.11) * mm, "end": v(-21.96, -23.3) * mm});
            skLineSegment(sketch, "E28.1.16.0", {"start": v(-18.67, -23.48) * mm, "end": v(-19.57, -25.33) * mm});
            skLineSegment(sketch, "E28.3.16.0", {"start": v(-19.57, -25.33) * mm, "end": v(-18.8, -25.89) * mm});
            skLineSegment(sketch, "E28.6.16.0", {"start": v(-18.05, -26.44) * mm, "end": v(-18.8, -25.89) * mm});
            skLineSegment(sketch, "E28.9.16.0", {"start": v(-16.57, -25.01) * mm, "end": v(-18.05, -26.44) * mm});
            skLineSegment(sketch, "E28.1.17.0", {"start": v(-14.77, -26.11) * mm, "end": v(-15.37, -28.08) * mm});
            skLineSegment(sketch, "E28.3.17.0", {"start": v(-15.37, -28.08) * mm, "end": v(-14.53, -28.51) * mm});
            skLineSegment(sketch, "E28.6.17.0", {"start": v(-13.69, -28.94) * mm, "end": v(-14.53, -28.51) * mm});
            skLineSegment(sketch, "E28.9.17.0", {"start": v(-12.45, -27.3) * mm, "end": v(-13.69, -28.94) * mm});
            skLineSegment(sketch, "E28.1.18.0", {"start": v(-10.5, -28.1) * mm, "end": v(-10.78, -30.14) * mm});
            skLineSegment(sketch, "E28.3.18.0", {"start": v(-10.78, -30.14) * mm, "end": v(-9.89, -30.43) * mm});
            skLineSegment(sketch, "E28.6.18.0", {"start": v(-9, -30.73) * mm, "end": v(-9.89, -30.43) * mm});
            skLineSegment(sketch, "E28.9.18.0", {"start": v(-8.03, -28.9) * mm, "end": v(-9, -30.73) * mm});
            skLineSegment(sketch, "E28.1.19.0", {"start": v(-5.97, -29.4) * mm, "end": v(-5.94, -31.46) * mm});
            skLineSegment(sketch, "E28.3.19.0", {"start": v(-5.94, -31.46) * mm, "end": v(-5, -31.6) * mm});
            skLineSegment(sketch, "E28.6.19.0", {"start": v(-4.08, -31.75) * mm, "end": v(-5, -31.6) * mm});
            skLineSegment(sketch, "E28.9.19.0", {"start": v(-3.4, -29.8) * mm, "end": v(-4.08, -31.75) * mm});
            skLineSegment(sketch, "E28.1.20.0", {"start": v(-1.3, -29.97) * mm, "end": v(-0.94, -32) * mm});
            skLineSegment(sketch, "E28.3.20.0", {"start": v(-0.94, -32) * mm, "end": v(0, -32) * mm});
            skLineSegment(sketch, "E28.6.20.0", {"start": v(0.94, -32) * mm, "end": v(0, -32) * mm});
            skLineSegment(sketch, "E28.9.20.0", {"start": v(1.3, -29.97) * mm, "end": v(0.94, -32) * mm});
            skLineSegment(sketch, "E28.1.21.0", {"start": v(3.4, -29.8) * mm, "end": v(4.08, -31.75) * mm});
            skLineSegment(sketch, "E28.3.21.0", {"start": v(4.08, -31.75) * mm, "end": v(5, -31.6) * mm});
            skLineSegment(sketch, "E28.6.21.0", {"start": v(5.94, -31.46) * mm, "end": v(5, -31.6) * mm});
            skLineSegment(sketch, "E28.9.21.0", {"start": v(5.97, -29.4) * mm, "end": v(5.94, -31.46) * mm});
            skLineSegment(sketch, "E28.1.22.0", {"start": v(8.03, -28.9) * mm, "end": v(9, -30.73) * mm});
            skLineSegment(sketch, "E28.3.22.0", {"start": v(9, -30.73) * mm, "end": v(9.89, -30.43) * mm});
            skLineSegment(sketch, "E28.6.22.0", {"start": v(10.78, -30.14) * mm, "end": v(9.89, -30.43) * mm});
            skLineSegment(sketch, "E28.9.22.0", {"start": v(10.5, -28.1) * mm, "end": v(10.78, -30.14) * mm});
            skLineSegment(sketch, "E28.1.23.0", {"start": v(12.45, -27.3) * mm, "end": v(13.69, -28.94) * mm});
            skLineSegment(sketch, "E28.3.23.0", {"start": v(13.69, -28.94) * mm, "end": v(14.53, -28.51) * mm});
            skLineSegment(sketch, "E28.6.23.0", {"start": v(15.37, -28.08) * mm, "end": v(14.53, -28.51) * mm});
            skLineSegment(sketch, "E28.9.23.0", {"start": v(14.77, -26.11) * mm, "end": v(15.37, -28.08) * mm});
            skLineSegment(sketch, "E28.1.24.0", {"start": v(16.57, -25.01) * mm, "end": v(18.05, -26.44) * mm});
            skLineSegment(sketch, "E28.3.24.0", {"start": v(18.05, -26.44) * mm, "end": v(18.8, -25.89) * mm});
            skLineSegment(sketch, "E28.6.24.0", {"start": v(19.57, -25.33) * mm, "end": v(18.8, -25.89) * mm});
            skLineSegment(sketch, "E28.9.24.0", {"start": v(18.67, -23.48) * mm, "end": v(19.57, -25.33) * mm});
            skLineSegment(sketch, "E28.1.25.0", {"start": v(20.27, -22.11) * mm, "end": v(21.96, -23.3) * mm});
            skLineSegment(sketch, "E28.3.25.0", {"start": v(21.96, -23.3) * mm, "end": v(22.63, -22.63) * mm});
            skLineSegment(sketch, "E28.6.25.0", {"start": v(23.3, -21.96) * mm, "end": v(22.63, -22.63) * mm});
            skLineSegment(sketch, "E28.9.25.0", {"start": v(22.11, -20.27) * mm, "end": v(23.3, -21.96) * mm});
            skLineSegment(sketch, "E28.1.26.0", {"start": v(23.48, -18.67) * mm, "end": v(25.33, -19.57) * mm});
            skLineSegment(sketch, "E28.3.26.0", {"start": v(25.33, -19.57) * mm, "end": v(25.89, -18.8) * mm});
            skLineSegment(sketch, "E28.6.26.0", {"start": v(26.44, -18.05) * mm, "end": v(25.89, -18.8) * mm});
            skLineSegment(sketch, "E28.9.26.0", {"start": v(25.01, -16.57) * mm, "end": v(26.44, -18.05) * mm});
            skLineSegment(sketch, "E28.1.27.0", {"start": v(26.11, -14.77) * mm, "end": v(28.08, -15.37) * mm});
            skLineSegment(sketch, "E28.3.27.0", {"start": v(28.08, -15.37) * mm, "end": v(28.51, -14.53) * mm});
            skLineSegment(sketch, "E28.6.27.0", {"start": v(28.94, -13.69) * mm, "end": v(28.51, -14.53) * mm});
            skLineSegment(sketch, "E28.9.27.0", {"start": v(27.3, -12.45) * mm, "end": v(28.94, -13.69) * mm});
            skLineSegment(sketch, "E28.1.28.0", {"start": v(28.1, -10.5) * mm, "end": v(30.14, -10.78) * mm});
            skLineSegment(sketch, "E28.3.28.0", {"start": v(30.14, -10.78) * mm, "end": v(30.43, -9.89) * mm});
            skLineSegment(sketch, "E28.6.28.0", {"start": v(30.73, -9) * mm, "end": v(30.43, -9.89) * mm});
            skLineSegment(sketch, "E28.9.28.0", {"start": v(28.9, -8.03) * mm, "end": v(30.73, -9) * mm});
            skLineSegment(sketch, "E28.1.29.0", {"start": v(29.4, -5.97) * mm, "end": v(31.46, -5.94) * mm});
            skLineSegment(sketch, "E28.3.29.0", {"start": v(31.46, -5.94) * mm, "end": v(31.6, -5) * mm});
            skLineSegment(sketch, "E28.6.29.0", {"start": v(31.75, -4.08) * mm, "end": v(31.6, -5) * mm});
            skLineSegment(sketch, "E28.9.29.0", {"start": v(29.8, -3.4) * mm, "end": v(31.75, -4.08) * mm});
            skLineSegment(sketch, "E28.1.30.0", {"start": v(29.97, -1.3) * mm, "end": v(32, -0.94) * mm});
            skLineSegment(sketch, "E28.3.30.0", {"start": v(32, -0.94) * mm, "end": v(32, 0) * mm});
            skLineSegment(sketch, "E28.6.30.0", {"start": v(32, 0.94) * mm, "end": v(32, 0) * mm});
            skLineSegment(sketch, "E28.9.30.0", {"start": v(29.97, 1.3) * mm, "end": v(32, 0.94) * mm});
            skLineSegment(sketch, "E28.1.31.0", {"start": v(29.8, 3.4) * mm, "end": v(31.75, 4.08) * mm});
            skLineSegment(sketch, "E28.3.31.0", {"start": v(31.75, 4.08) * mm, "end": v(31.6, 5) * mm});
            skLineSegment(sketch, "E28.6.31.0", {"start": v(31.46, 5.94) * mm, "end": v(31.6, 5) * mm});
            skLineSegment(sketch, "E28.9.31.0", {"start": v(29.4, 5.97) * mm, "end": v(31.46, 5.94) * mm});
            skLineSegment(sketch, "E28.1.32.0", {"start": v(28.9, 8.03) * mm, "end": v(30.73, 9) * mm});
            skLineSegment(sketch, "E28.3.32.0", {"start": v(30.73, 9) * mm, "end": v(30.43, 9.89) * mm});
            skLineSegment(sketch, "E28.6.32.0", {"start": v(30.14, 10.78) * mm, "end": v(30.43, 9.89) * mm});
            skLineSegment(sketch, "E28.9.32.0", {"start": v(28.1, 10.5) * mm, "end": v(30.14, 10.78) * mm});
            skLineSegment(sketch, "E28.1.33.0", {"start": v(27.3, 12.45) * mm, "end": v(28.94, 13.69) * mm});
            skLineSegment(sketch, "E28.3.33.0", {"start": v(28.94, 13.69) * mm, "end": v(28.51, 14.53) * mm});
            skLineSegment(sketch, "E28.6.33.0", {"start": v(28.08, 15.37) * mm, "end": v(28.51, 14.53) * mm});
            skLineSegment(sketch, "E28.9.33.0", {"start": v(26.11, 14.77) * mm, "end": v(28.08, 15.37) * mm});
            skLineSegment(sketch, "E28.1.34.0", {"start": v(25.01, 16.57) * mm, "end": v(26.44, 18.05) * mm});
            skLineSegment(sketch, "E28.3.34.0", {"start": v(26.44, 18.05) * mm, "end": v(25.89, 18.8) * mm});
            skLineSegment(sketch, "E28.6.34.0", {"start": v(25.33, 19.57) * mm, "end": v(25.89, 18.8) * mm});
            skLineSegment(sketch, "E28.9.34.0", {"start": v(23.48, 18.67) * mm, "end": v(25.33, 19.57) * mm});
            skLineSegment(sketch, "E28.1.35.0", {"start": v(22.11, 20.27) * mm, "end": v(23.3, 21.96) * mm});
            skLineSegment(sketch, "E28.3.35.0", {"start": v(23.3, 21.96) * mm, "end": v(22.63, 22.63) * mm});
            skLineSegment(sketch, "E28.6.35.0", {"start": v(21.96, 23.3) * mm, "end": v(22.63, 22.63) * mm});
            skLineSegment(sketch, "E28.9.35.0", {"start": v(20.27, 22.11) * mm, "end": v(21.96, 23.3) * mm});
            skLineSegment(sketch, "E28.1.36.0", {"start": v(18.67, 23.48) * mm, "end": v(19.57, 25.33) * mm});
            skLineSegment(sketch, "E28.3.36.0", {"start": v(19.57, 25.33) * mm, "end": v(18.8, 25.89) * mm});
            skLineSegment(sketch, "E28.6.36.0", {"start": v(18.05, 26.44) * mm, "end": v(18.8, 25.89) * mm});
            skLineSegment(sketch, "E28.9.36.0", {"start": v(16.57, 25.01) * mm, "end": v(18.05, 26.44) * mm});
            skLineSegment(sketch, "E28.1.37.0", {"start": v(14.77, 26.11) * mm, "end": v(15.37, 28.08) * mm});
            skLineSegment(sketch, "E28.3.37.0", {"start": v(15.37, 28.08) * mm, "end": v(14.53, 28.51) * mm});
            skLineSegment(sketch, "E28.6.37.0", {"start": v(13.69, 28.94) * mm, "end": v(14.53, 28.51) * mm});
            skLineSegment(sketch, "E28.9.37.0", {"start": v(12.45, 27.3) * mm, "end": v(13.69, 28.94) * mm});
            skLineSegment(sketch, "E28.1.38.0", {"start": v(10.5, 28.1) * mm, "end": v(10.78, 30.14) * mm});
            skLineSegment(sketch, "E28.3.38.0", {"start": v(10.78, 30.14) * mm, "end": v(9.89, 30.43) * mm});
            skLineSegment(sketch, "E28.6.38.0", {"start": v(9, 30.73) * mm, "end": v(9.89, 30.43) * mm});
            skLineSegment(sketch, "E28.9.38.0", {"start": v(8.03, 28.9) * mm, "end": v(9, 30.73) * mm});
            skLineSegment(sketch, "E28.1.39.0", {"start": v(5.97, 29.4) * mm, "end": v(5.94, 31.46) * mm});
            skLineSegment(sketch, "E28.3.39.0", {"start": v(5.94, 31.46) * mm, "end": v(5, 31.6) * mm});
            skLineSegment(sketch, "E28.6.39.0", {"start": v(4.08, 31.75) * mm, "end": v(5, 31.6) * mm});
            skLineSegment(sketch, "E28.9.39.0", {"start": v(3.4, 29.8) * mm, "end": v(4.08, 31.75) * mm});
            skSolve(sketch);
        }
        {
            var Q0;
            Q0 = qSketchRegion(id + "F14", true);
            extrude(context, id + "F15", {"entities" : qUnion([Q0]), "operationType" : NewBodyOperationType.ADD, "depth" : 4 * mm, "offsetDistance" : 25 * mm});
        }
        {
            var Q0;
            Q0=makeQuery(id+"F7.opExtrude","CAP_FACE",FACE,{"disambiguationData":[OSD([sQuery(id+"F0.wireOp",EDGE,"E0")])],"isStart":false});
            var sketch = newSketch(context, id + "F16", { "sketchPlane" : qUnion([Q0])});
            skCircle(sketch, "E29", {"center": v(40, 0) * mm, "radius": 7.5 * mm});
            skLineSegment(sketch, "E30", {"start": v(40, 0) * mm, "end": v(40, 7.5) * mm, "construction": true});
            skLineSegment(sketch, "E31", {"start": v(38.68, 7.38) * mm, "end": v(39.06, 9.5) * mm});
            skLineSegment(sketch, "E32", {"start": v(39.06, 9.5) * mm, "end": v(40.94, 9.5) * mm});
            skLineSegment(sketch, "E33.MirrorCS", {"start": v(41.32, 7.38) * mm, "end": v(40.94, 9.5) * mm});
            skLineSegment(sketch, "E34.1.0", {"start": v(36.72, 6.75) * mm, "end": v(35.18, 8.24) * mm});
            skLineSegment(sketch, "E34.1.1", {"start": v(33.65, 7.13) * mm, "end": v(35.18, 8.24) * mm});
            skLineSegment(sketch, "E34.1.2", {"start": v(34.6, 5.2) * mm, "end": v(33.65, 7.13) * mm});
            skLineSegment(sketch, "E34.2.0", {"start": v(33.38, 3.53) * mm, "end": v(31.26, 3.83) * mm});
            skLineSegment(sketch, "E34.2.1", {"start": v(30.67, 2.04) * mm, "end": v(31.26, 3.83) * mm});
            skLineSegment(sketch, "E34.2.2", {"start": v(32.57, 1.03) * mm, "end": v(30.67, 2.04) * mm});
            skLineSegment(sketch, "E35.1.3.0", {"start": v(32.57, -1.03) * mm, "end": v(30.67, -2.04) * mm});
            skLineSegment(sketch, "E35.3.3.0", {"start": v(31.26, -3.83) * mm, "end": v(30.67, -2.04) * mm});
            skLineSegment(sketch, "E35.6.3.0", {"start": v(33.38, -3.53) * mm, "end": v(31.26, -3.83) * mm});
            skLineSegment(sketch, "E35.1.4.0", {"start": v(34.6, -5.2) * mm, "end": v(33.65, -7.13) * mm});
            skLineSegment(sketch, "E35.3.4.0", {"start": v(35.18, -8.24) * mm, "end": v(33.65, -7.13) * mm});
            skLineSegment(sketch, "E35.6.4.0", {"start": v(36.72, -6.75) * mm, "end": v(35.18, -8.24) * mm});
            skLineSegment(sketch, "E35.1.5.0", {"start": v(38.68, -7.38) * mm, "end": v(39.06, -9.5) * mm});
            skLineSegment(sketch, "E35.3.5.0", {"start": v(40.94, -9.5) * mm, "end": v(39.06, -9.5) * mm});
            skLineSegment(sketch, "E35.6.5.0", {"start": v(41.32, -7.38) * mm, "end": v(40.94, -9.5) * mm});
            skLineSegment(sketch, "E35.1.6.0", {"start": v(43.28, -6.75) * mm, "end": v(44.82, -8.24) * mm});
            skLineSegment(sketch, "E35.3.6.0", {"start": v(46.35, -7.13) * mm, "end": v(44.82, -8.24) * mm});
            skLineSegment(sketch, "E35.6.6.0", {"start": v(45.4, -5.2) * mm, "end": v(46.35, -7.13) * mm});
            skLineSegment(sketch, "E35.1.7.0", {"start": v(46.62, -3.53) * mm, "end": v(48.74, -3.83) * mm});
            skLineSegment(sketch, "E35.3.7.0", {"start": v(49.33, -2.04) * mm, "end": v(48.74, -3.83) * mm});
            skLineSegment(sketch, "E35.6.7.0", {"start": v(47.43, -1.03) * mm, "end": v(49.33, -2.04) * mm});
            skLineSegment(sketch, "E35.1.8.0", {"start": v(47.43, 1.03) * mm, "end": v(49.33, 2.04) * mm});
            skLineSegment(sketch, "E35.3.8.0", {"start": v(48.74, 3.83) * mm, "end": v(49.33, 2.04) * mm});
            skLineSegment(sketch, "E35.6.8.0", {"start": v(46.62, 3.53) * mm, "end": v(48.74, 3.83) * mm});
            skLineSegment(sketch, "E35.1.9.0", {"start": v(45.4, 5.2) * mm, "end": v(46.35, 7.13) * mm});
            skLineSegment(sketch, "E35.3.9.0", {"start": v(44.82, 8.24) * mm, "end": v(46.35, 7.13) * mm});
            skLineSegment(sketch, "E35.6.9.0", {"start": v(43.28, 6.75) * mm, "end": v(44.82, 8.24) * mm});
            skSolve(sketch);
        }
        {
            var Q0;
            Q0 = qSketchRegion(id + "F16", true);
            extrude(context, id + "F17", {"entities" : qUnion([Q0]), "operationType" : NewBodyOperationType.ADD, "depth" : 4 * mm, "offsetDistance" : 25 * mm});
        }
        {
            var Q0;
            Q0=makeQuery(id+"F17.opExtrude","CAP_FACE",FACE,{"disambiguationData":[OSD([sQuery(id+"F16.wireOp",EDGE,"E29"),sQuery(id+"F16.wireOp",EDGE,"E31"),sQuery(id+"F16.wireOp",EDGE,"E32"),sQuery(id+"F16.wireOp",EDGE,"E33.MirrorCS"),sQuery(id+"F16.wireOp",EDGE,"E34.1.0"),sQuery(id+"F16.wireOp",EDGE,"E34.1.1"),sQuery(id+"F16.wireOp",EDGE,"E34.1.2"),sQuery(id+"F16.wireOp",EDGE,"E34.2.0"),sQuery(id+"F16.wireOp",EDGE,"E34.2.1"),sQuery(id+"F16.wireOp",EDGE,"E34.2.2"),sQuery(id+"F16.wireOp",EDGE,"E35.1.3.0"),sQuery(id+"F16.wireOp",EDGE,"E35.3.3.0"),sQuery(id+"F16.wireOp",EDGE,"E35.6.3.0"),sQuery(id+"F16.wireOp",EDGE,"E35.1.4.0"),sQuery(id+"F16.wireOp",EDGE,"E35.3.4.0"),sQuery(id+"F16.wireOp",EDGE,"E35.6.4.0"),sQuery(id+"F16.wireOp",EDGE,"E35.1.5.0"),sQuery(id+"F16.wireOp",EDGE,"E35.3.5.0"),sQuery(id+"F16.wireOp",EDGE,"E35.6.5.0"),sQuery(id+"F16.wireOp",EDGE,"E35.1.6.0"),sQuery(id+"F16.wireOp",EDGE,"E35.3.6.0"),sQuery(id+"F16.wireOp",EDGE,"E35.6.6.0"),sQuery(id+"F16.wireOp",EDGE,"E35.1.7.0"),sQuery(id+"F16.wireOp",EDGE,"E35.3.7.0"),sQuery(id+"F16.wireOp",EDGE,"E35.6.7.0"),sQuery(id+"F16.wireOp",EDGE,"E35.1.8.0"),sQuery(id+"F16.wireOp",EDGE,"E35.3.8.0"),sQuery(id+"F16.wireOp",EDGE,"E35.6.8.0"),sQuery(id+"F16.wireOp",EDGE,"E35.1.9.0"),sQuery(id+"F16.wireOp",EDGE,"E35.3.9.0"),sQuery(id+"F16.wireOp",EDGE,"E35.6.9.0")])],"isStart":false});
            var sketch = newSketch(context, id + "F18", { "sketchPlane" : qUnion([Q0])});
            skCircle(sketch, "E36.0", {"center": v(40, 0) * mm, "radius": 3 * mm});
            skSolve(sketch);
        }
        {
            var Q0;
            Q0 = qSketchRegion(id + "F18", true);
            extrude(context, id + "F19", {"entities" : qUnion([Q0]), "operationType" : NewBodyOperationType.ADD, "depth" : 2 * mm, "offsetDistance" : 25 * mm});
        }
        {
            var Q0;
            Q0=makeQuery(id+"F19.opExtrude","CAP_FACE",FACE,{"disambiguationData":[OSD([sQuery(id+"F18.wireOp",EDGE,"E36.0")])],"isStart":false});
            var sketch = newSketch(context, id + "F20", { "sketchPlane" : qUnion([Q0])});
            skCircle(sketch, "E37", {"center": v(0, 0) * mm, "radius": 98 * mm});
            skCircle(sketch, "E38.0", {"center": v(0, 0) * mm, "radius": 5 * mm});
            skSolve(sketch);
        }
        {
            var Q0;
            Q0 = qSketchRegion(id + "F20", true);
            extrude(context, id + "F21", {"entities" : qUnion([Q0]), "depth" : 1 * mm, "offsetDistance" : 25 * mm});
        }
        {
            var Q0;
            Q0=makeQuery(id+"F21.opExtrude","SWEPT_BODY",BODY,{"disambiguationData":[OSD([sQuery(id+"F20.wireOp",EDGE,"E37"),sQuery(id+"F20.wireOp",EDGE,"E38.0")])]});
            var Q1;
            Q1=makeQuery(id+"F1.opExtrude","SWEPT_BODY",BODY,{"disambiguationData":[OSD([sQuery(id+"F0.wireOp",EDGE,"E0")])]});
            booleanBodies(context, id + "F22", {"operationType" : BooleanOperationType.SUBTRACTION, "tools" : qUnion([Q0]), "targets" : qUnion([Q1]), "keepTools" : true});
        }
        {
            var Q0;
            Q0=makeQuery(id+"F21.opExtrude","CAP_FACE",FACE,{"disambiguationData":[OSD([sQuery(id+"F20.wireOp",EDGE,"E37"),sQuery(id+"F20.wireOp",EDGE,"E38.0")])],"isStart":true});
            var sketch = newSketch(context, id + "F23", { "sketchPlane" : qUnion([Q0])});
            skCircle(sketch, "E39.0", {"center": v(-40, 0) * mm, "radius": 3 * mm});
            skCircle(sketch, "E40", {"center": v(-40, 0) * mm, "radius": 5 * mm});
            skSolve(sketch);
        }
        {
            var Q0;
            Q0 = qSketchRegion(id + "F23", true);
            extrude(context, id + "F24", {"entities" : qUnion([Q0]), "operationType" : NewBodyOperationType.ADD, "endBound" : BoundingType.UP_TO_NEXT, "depth" : 25 * mm, "offsetDistance" : 25 * mm});
        }
        {
            var Q0;
            Q0=makeQuery(id+"F21.opExtrude","CAP_FACE",FACE,{"disambiguationData":[OSD([sQuery(id+"F20.wireOp",EDGE,"E37"),sQuery(id+"F20.wireOp",EDGE,"E38.0")])],"isStart":false});
            var sketch = newSketch(context, id + "F25", { "sketchPlane" : qUnion([Q0])});
            skLineSegment(sketch, "E41.bottom", {"start": v(-1.5, 71) * mm, "end": v(1.5, 71) * mm});
            skLineSegment(sketch, "E41.top", {"start": v(-1.5, 91) * mm, "end": v(1.5, 91) * mm});
            skLineSegment(sketch, "E41.left", {"start": v(-1.5, 71) * mm, "end": v(-1.5, 91) * mm});
            skLineSegment(sketch, "E41.right", {"start": v(1.5, 71) * mm, "end": v(1.5, 91) * mm});
            skPoint(sketch, "E41.middle", {"position": v(0, 81) * mm});
            skLineSegment(sketch, "E42.1.0", {"start": v(-34.2, 62.24) * mm, "end": v(-44.2, 79.56) * mm});
            skLineSegment(sketch, "E42.1.1", {"start": v(-46.8, 78.06) * mm, "end": v(-44.2, 79.56) * mm});
            skLineSegment(sketch, "E42.1.2", {"start": v(-36.8, 60.74) * mm, "end": v(-46.8, 78.06) * mm});
            skLineSegment(sketch, "E42.1.3", {"start": v(-36.8, 60.74) * mm, "end": v(-34.2, 62.24) * mm});
            skLineSegment(sketch, "E42.2.0", {"start": v(-60.74, 36.8) * mm, "end": v(-78.06, 46.8) * mm});
            skLineSegment(sketch, "E42.2.1", {"start": v(-79.56, 44.2) * mm, "end": v(-78.06, 46.8) * mm});
            skLineSegment(sketch, "E42.2.2", {"start": v(-62.24, 34.2) * mm, "end": v(-79.56, 44.2) * mm});
            skLineSegment(sketch, "E42.2.3", {"start": v(-62.24, 34.2) * mm, "end": v(-60.74, 36.8) * mm});
            skPoint(sketch, "E42.center", {"position": v(0, 0) * mm});
            skLineSegment(sketch, "E43.1.3.0", {"start": v(-71, 1.5) * mm, "end": v(-91, 1.5) * mm});
            skLineSegment(sketch, "E43.3.3.0", {"start": v(-91, -1.5) * mm, "end": v(-91, 1.5) * mm});
            skLineSegment(sketch, "E43.6.3.0", {"start": v(-71, -1.5) * mm, "end": v(-91, -1.5) * mm});
            skLineSegment(sketch, "E43.9.3.0", {"start": v(-71, -1.5) * mm, "end": v(-71, 1.5) * mm});
            skLineSegment(sketch, "E43.1.4.0", {"start": v(-62.24, -34.2) * mm, "end": v(-79.56, -44.2) * mm});
            skLineSegment(sketch, "E43.3.4.0", {"start": v(-78.06, -46.8) * mm, "end": v(-79.56, -44.2) * mm});
            skLineSegment(sketch, "E43.6.4.0", {"start": v(-60.74, -36.8) * mm, "end": v(-78.06, -46.8) * mm});
            skLineSegment(sketch, "E43.9.4.0", {"start": v(-60.74, -36.8) * mm, "end": v(-62.24, -34.2) * mm});
            skLineSegment(sketch, "E43.1.5.0", {"start": v(-36.8, -60.74) * mm, "end": v(-46.8, -78.06) * mm});
            skLineSegment(sketch, "E43.3.5.0", {"start": v(-44.2, -79.56) * mm, "end": v(-46.8, -78.06) * mm});
            skLineSegment(sketch, "E43.6.5.0", {"start": v(-34.2, -62.24) * mm, "end": v(-44.2, -79.56) * mm});
            skLineSegment(sketch, "E43.9.5.0", {"start": v(-34.2, -62.24) * mm, "end": v(-36.8, -60.74) * mm});
            skLineSegment(sketch, "E43.1.6.0", {"start": v(-1.5, -71) * mm, "end": v(-1.5, -91) * mm});
            skLineSegment(sketch, "E43.3.6.0", {"start": v(1.5, -91) * mm, "end": v(-1.5, -91) * mm});
            skLineSegment(sketch, "E43.6.6.0", {"start": v(1.5, -71) * mm, "end": v(1.5, -91) * mm});
            skLineSegment(sketch, "E43.9.6.0", {"start": v(1.5, -71) * mm, "end": v(-1.5, -71) * mm});
            skLineSegment(sketch, "E43.1.7.0", {"start": v(34.2, -62.24) * mm, "end": v(44.2, -79.56) * mm});
            skLineSegment(sketch, "E43.3.7.0", {"start": v(46.8, -78.06) * mm, "end": v(44.2, -79.56) * mm});
            skLineSegment(sketch, "E43.6.7.0", {"start": v(36.8, -60.74) * mm, "end": v(46.8, -78.06) * mm});
            skLineSegment(sketch, "E43.9.7.0", {"start": v(36.8, -60.74) * mm, "end": v(34.2, -62.24) * mm});
            skLineSegment(sketch, "E43.1.8.0", {"start": v(60.74, -36.8) * mm, "end": v(78.06, -46.8) * mm});
            skLineSegment(sketch, "E43.3.8.0", {"start": v(79.56, -44.2) * mm, "end": v(78.06, -46.8) * mm});
            skLineSegment(sketch, "E43.6.8.0", {"start": v(62.24, -34.2) * mm, "end": v(79.56, -44.2) * mm});
            skLineSegment(sketch, "E43.9.8.0", {"start": v(62.24, -34.2) * mm, "end": v(60.74, -36.8) * mm});
            skLineSegment(sketch, "E43.1.9.0", {"start": v(71, -1.5) * mm, "end": v(91, -1.5) * mm});
            skLineSegment(sketch, "E43.3.9.0", {"start": v(91, 1.5) * mm, "end": v(91, -1.5) * mm});
            skLineSegment(sketch, "E43.6.9.0", {"start": v(71, 1.5) * mm, "end": v(91, 1.5) * mm});
            skLineSegment(sketch, "E43.9.9.0", {"start": v(71, 1.5) * mm, "end": v(71, -1.5) * mm});
            skLineSegment(sketch, "E43.1.10.0", {"start": v(62.24, 34.2) * mm, "end": v(79.56, 44.2) * mm});
            skLineSegment(sketch, "E43.3.10.0", {"start": v(78.06, 46.8) * mm, "end": v(79.56, 44.2) * mm});
            skLineSegment(sketch, "E43.6.10.0", {"start": v(60.74, 36.8) * mm, "end": v(78.06, 46.8) * mm});
            skLineSegment(sketch, "E43.9.10.0", {"start": v(60.74, 36.8) * mm, "end": v(62.24, 34.2) * mm});
            skLineSegment(sketch, "E43.1.11.0", {"start": v(36.8, 60.74) * mm, "end": v(46.8, 78.06) * mm});
            skLineSegment(sketch, "E43.3.11.0", {"start": v(44.2, 79.56) * mm, "end": v(46.8, 78.06) * mm});
            skLineSegment(sketch, "E43.6.11.0", {"start": v(34.2, 62.24) * mm, "end": v(44.2, 79.56) * mm});
            skLineSegment(sketch, "E43.9.11.0", {"start": v(34.2, 62.24) * mm, "end": v(36.8, 60.74) * mm});
            skSolve(sketch);
        }
        {
            var Q0;
            Q0 = qSketchRegion(id + "F25", true);
            extrude(context, id + "F26", {"entities" : qUnion([Q0]), "operationType" : NewBodyOperationType.REMOVE, "oppositeDirection" : true, "depth" : 0.5 * mm, "offsetDistance" : 25 * mm});
        }
        {
            var Q0;
            Q0=makeQuery(id+"F21.opExtrude","CAP_FACE",FACE,{"disambiguationData":[OSD([sQuery(id+"F20.wireOp",EDGE,"E37"),sQuery(id+"F20.wireOp",EDGE,"E38.0")])],"isStart":false});
            var sketch = newSketch(context, id + "F27", { "sketchPlane" : qUnion([Q0])});
            skLineSegment(sketch, "E44.bottom", {"start": v(-0.75, 78.5) * mm, "end": v(0.75, 78.5) * mm});
            skLineSegment(sketch, "E44.top", {"start": v(-0.75, 90.5) * mm, "end": v(0.75, 90.5) * mm});
            skLineSegment(sketch, "E44.left", {"start": v(-0.75, 78.5) * mm, "end": v(-0.75, 90.5) * mm});
            skLineSegment(sketch, "E44.right", {"start": v(0.75, 78.5) * mm, "end": v(0.75, 90.5) * mm});
            skPoint(sketch, "E44.middle", {"position": v(0, 84.5) * mm});
            skLineSegment(sketch, "E45.1.0", {"start": v(-10.2, 89.93) * mm, "end": v(-8.71, 90.08) * mm});
            skLineSegment(sketch, "E45.1.1", {"start": v(-7.46, 78.15) * mm, "end": v(-8.71, 90.08) * mm});
            skLineSegment(sketch, "E45.1.2", {"start": v(-8.95, 78) * mm, "end": v(-10.2, 89.93) * mm});
            skLineSegment(sketch, "E45.1.3", {"start": v(-8.95, 78) * mm, "end": v(-7.46, 78.15) * mm});
            skLineSegment(sketch, "E45.2.0", {"start": v(-19.55, 88.37) * mm, "end": v(-18.08, 88.68) * mm});
            skLineSegment(sketch, "E45.2.1", {"start": v(-15.59, 76.94) * mm, "end": v(-18.08, 88.68) * mm});
            skLineSegment(sketch, "E45.2.2", {"start": v(-17.05, 76.63) * mm, "end": v(-19.55, 88.37) * mm});
            skLineSegment(sketch, "E45.2.3", {"start": v(-17.05, 76.63) * mm, "end": v(-15.59, 76.94) * mm});
            skPoint(sketch, "E45.center", {"position": v(0, 0) * mm});
            skLineSegment(sketch, "E46.1.3.0", {"start": v(-28.68, 85.84) * mm, "end": v(-27.25, 86.3) * mm});
            skLineSegment(sketch, "E46.3.3.0", {"start": v(-23.54, 74.89) * mm, "end": v(-27.25, 86.3) * mm});
            skLineSegment(sketch, "E46.6.3.0", {"start": v(-24.97, 74.43) * mm, "end": v(-28.68, 85.84) * mm});
            skLineSegment(sketch, "E46.9.3.0", {"start": v(-24.97, 74.43) * mm, "end": v(-23.54, 74.89) * mm});
            skLineSegment(sketch, "E46.1.4.0", {"start": v(-37.5, 82.37) * mm, "end": v(-36.12, 82.98) * mm});
            skLineSegment(sketch, "E46.3.4.0", {"start": v(-31.24, 72.02) * mm, "end": v(-36.12, 82.98) * mm});
            skLineSegment(sketch, "E46.6.4.0", {"start": v(-32.61, 71.4) * mm, "end": v(-37.5, 82.37) * mm});
            skLineSegment(sketch, "E46.9.4.0", {"start": v(-32.61, 71.4) * mm, "end": v(-31.24, 72.02) * mm});
            skLineSegment(sketch, "E46.1.5.0", {"start": v(-45.9, 78) * mm, "end": v(-44.6, 78.75) * mm});
            skLineSegment(sketch, "E46.3.5.0", {"start": v(-38.6, 68.36) * mm, "end": v(-44.6, 78.75) * mm});
            skLineSegment(sketch, "E46.6.5.0", {"start": v(-39.9, 67.6) * mm, "end": v(-45.9, 78) * mm});
            skLineSegment(sketch, "E46.9.5.0", {"start": v(-39.9, 67.6) * mm, "end": v(-38.6, 68.36) * mm});
            skLineSegment(sketch, "E46.1.6.0", {"start": v(-53.8, 72.78) * mm, "end": v(-52.59, 73.66) * mm});
            skLineSegment(sketch, "E46.3.6.0", {"start": v(-45.53, 63.95) * mm, "end": v(-52.59, 73.66) * mm});
            skLineSegment(sketch, "E46.6.6.0", {"start": v(-46.75, 63.07) * mm, "end": v(-53.8, 72.78) * mm});
            skLineSegment(sketch, "E46.9.6.0", {"start": v(-46.75, 63.07) * mm, "end": v(-45.53, 63.95) * mm});
            skLineSegment(sketch, "E46.1.7.0", {"start": v(-61.11, 66.75) * mm, "end": v(-60, 67.76) * mm});
            skLineSegment(sketch, "E46.3.7.0", {"start": v(-51.97, 58.84) * mm, "end": v(-60, 67.76) * mm});
            skLineSegment(sketch, "E46.6.7.0", {"start": v(-53.08, 57.84) * mm, "end": v(-61.11, 66.75) * mm});
            skLineSegment(sketch, "E46.9.7.0", {"start": v(-53.08, 57.84) * mm, "end": v(-51.97, 58.84) * mm});
            skLineSegment(sketch, "E46.1.8.0", {"start": v(-67.76, 60) * mm, "end": v(-66.75, 61.11) * mm});
            skLineSegment(sketch, "E46.3.8.0", {"start": v(-57.84, 53.08) * mm, "end": v(-66.75, 61.11) * mm});
            skLineSegment(sketch, "E46.6.8.0", {"start": v(-58.84, 51.97) * mm, "end": v(-67.76, 60) * mm});
            skLineSegment(sketch, "E46.9.8.0", {"start": v(-58.84, 51.97) * mm, "end": v(-57.84, 53.08) * mm});
            skLineSegment(sketch, "E46.1.9.0", {"start": v(-73.66, 52.59) * mm, "end": v(-72.78, 53.8) * mm});
            skLineSegment(sketch, "E46.3.9.0", {"start": v(-63.07, 46.75) * mm, "end": v(-72.78, 53.8) * mm});
            skLineSegment(sketch, "E46.6.9.0", {"start": v(-63.95, 45.53) * mm, "end": v(-73.66, 52.59) * mm});
            skLineSegment(sketch, "E46.9.9.0", {"start": v(-63.95, 45.53) * mm, "end": v(-63.07, 46.75) * mm});
            skLineSegment(sketch, "E46.1.10.0", {"start": v(-78.75, 44.6) * mm, "end": v(-78, 45.9) * mm});
            skLineSegment(sketch, "E46.3.10.0", {"start": v(-67.6, 39.9) * mm, "end": v(-78, 45.9) * mm});
            skLineSegment(sketch, "E46.6.10.0", {"start": v(-68.36, 38.6) * mm, "end": v(-78.75, 44.6) * mm});
            skLineSegment(sketch, "E46.9.10.0", {"start": v(-68.36, 38.6) * mm, "end": v(-67.6, 39.9) * mm});
            skLineSegment(sketch, "E46.1.11.0", {"start": v(-82.98, 36.12) * mm, "end": v(-82.37, 37.5) * mm});
            skLineSegment(sketch, "E46.3.11.0", {"start": v(-71.4, 32.61) * mm, "end": v(-82.37, 37.5) * mm});
            skLineSegment(sketch, "E46.6.11.0", {"start": v(-72.02, 31.24) * mm, "end": v(-82.98, 36.12) * mm});
            skLineSegment(sketch, "E46.9.11.0", {"start": v(-72.02, 31.24) * mm, "end": v(-71.4, 32.61) * mm});
            skLineSegment(sketch, "E46.1.12.0", {"start": v(-86.3, 27.25) * mm, "end": v(-85.84, 28.68) * mm});
            skLineSegment(sketch, "E46.3.12.0", {"start": v(-74.43, 24.97) * mm, "end": v(-85.84, 28.68) * mm});
            skLineSegment(sketch, "E46.6.12.0", {"start": v(-74.89, 23.54) * mm, "end": v(-86.3, 27.25) * mm});
            skLineSegment(sketch, "E46.9.12.0", {"start": v(-74.89, 23.54) * mm, "end": v(-74.43, 24.97) * mm});
            skLineSegment(sketch, "E46.1.13.0", {"start": v(-88.68, 18.08) * mm, "end": v(-88.37, 19.55) * mm});
            skLineSegment(sketch, "E46.3.13.0", {"start": v(-76.63, 17.05) * mm, "end": v(-88.37, 19.55) * mm});
            skLineSegment(sketch, "E46.6.13.0", {"start": v(-76.94, 15.59) * mm, "end": v(-88.68, 18.08) * mm});
            skLineSegment(sketch, "E46.9.13.0", {"start": v(-76.94, 15.59) * mm, "end": v(-76.63, 17.05) * mm});
            skLineSegment(sketch, "E46.1.14.0", {"start": v(-90.08, 8.71) * mm, "end": v(-89.93, 10.2) * mm});
            skLineSegment(sketch, "E46.3.14.0", {"start": v(-78, 8.95) * mm, "end": v(-89.93, 10.2) * mm});
            skLineSegment(sketch, "E46.6.14.0", {"start": v(-78.15, 7.46) * mm, "end": v(-90.08, 8.71) * mm});
            skLineSegment(sketch, "E46.9.14.0", {"start": v(-78.15, 7.46) * mm, "end": v(-78, 8.95) * mm});
            skLineSegment(sketch, "E46.1.15.0", {"start": v(-90.5, -0.75) * mm, "end": v(-90.5, 0.75) * mm});
            skLineSegment(sketch, "E46.3.15.0", {"start": v(-78.5, 0.75) * mm, "end": v(-90.5, 0.75) * mm});
            skLineSegment(sketch, "E46.6.15.0", {"start": v(-78.5, -0.75) * mm, "end": v(-90.5, -0.75) * mm});
            skLineSegment(sketch, "E46.9.15.0", {"start": v(-78.5, -0.75) * mm, "end": v(-78.5, 0.75) * mm});
            skLineSegment(sketch, "E46.1.16.0", {"start": v(-89.93, -10.2) * mm, "end": v(-90.08, -8.71) * mm});
            skLineSegment(sketch, "E46.3.16.0", {"start": v(-78.15, -7.46) * mm, "end": v(-90.08, -8.71) * mm});
            skLineSegment(sketch, "E46.6.16.0", {"start": v(-78, -8.95) * mm, "end": v(-89.93, -10.2) * mm});
            skLineSegment(sketch, "E46.9.16.0", {"start": v(-78, -8.95) * mm, "end": v(-78.15, -7.46) * mm});
            skLineSegment(sketch, "E46.1.17.0", {"start": v(-88.37, -19.55) * mm, "end": v(-88.68, -18.08) * mm});
            skLineSegment(sketch, "E46.3.17.0", {"start": v(-76.94, -15.59) * mm, "end": v(-88.68, -18.08) * mm});
            skLineSegment(sketch, "E46.6.17.0", {"start": v(-76.63, -17.05) * mm, "end": v(-88.37, -19.55) * mm});
            skLineSegment(sketch, "E46.9.17.0", {"start": v(-76.63, -17.05) * mm, "end": v(-76.94, -15.59) * mm});
            skLineSegment(sketch, "E46.1.18.0", {"start": v(-85.84, -28.68) * mm, "end": v(-86.3, -27.25) * mm});
            skLineSegment(sketch, "E46.3.18.0", {"start": v(-74.89, -23.54) * mm, "end": v(-86.3, -27.25) * mm});
            skLineSegment(sketch, "E46.6.18.0", {"start": v(-74.43, -24.97) * mm, "end": v(-85.84, -28.68) * mm});
            skLineSegment(sketch, "E46.9.18.0", {"start": v(-74.43, -24.97) * mm, "end": v(-74.89, -23.54) * mm});
            skLineSegment(sketch, "E46.1.19.0", {"start": v(-82.37, -37.5) * mm, "end": v(-82.98, -36.12) * mm});
            skLineSegment(sketch, "E46.3.19.0", {"start": v(-72.02, -31.24) * mm, "end": v(-82.98, -36.12) * mm});
            skLineSegment(sketch, "E46.6.19.0", {"start": v(-71.4, -32.61) * mm, "end": v(-82.37, -37.5) * mm});
            skLineSegment(sketch, "E46.9.19.0", {"start": v(-71.4, -32.61) * mm, "end": v(-72.02, -31.24) * mm});
            skLineSegment(sketch, "E46.1.20.0", {"start": v(-78, -45.9) * mm, "end": v(-78.75, -44.6) * mm});
            skLineSegment(sketch, "E46.3.20.0", {"start": v(-68.36, -38.6) * mm, "end": v(-78.75, -44.6) * mm});
            skLineSegment(sketch, "E46.6.20.0", {"start": v(-67.6, -39.9) * mm, "end": v(-78, -45.9) * mm});
            skLineSegment(sketch, "E46.9.20.0", {"start": v(-67.6, -39.9) * mm, "end": v(-68.36, -38.6) * mm});
            skLineSegment(sketch, "E46.1.21.0", {"start": v(-72.78, -53.8) * mm, "end": v(-73.66, -52.59) * mm});
            skLineSegment(sketch, "E46.3.21.0", {"start": v(-63.95, -45.53) * mm, "end": v(-73.66, -52.59) * mm});
            skLineSegment(sketch, "E46.6.21.0", {"start": v(-63.07, -46.75) * mm, "end": v(-72.78, -53.8) * mm});
            skLineSegment(sketch, "E46.9.21.0", {"start": v(-63.07, -46.75) * mm, "end": v(-63.95, -45.53) * mm});
            skLineSegment(sketch, "E46.1.22.0", {"start": v(-66.75, -61.11) * mm, "end": v(-67.76, -60) * mm});
            skLineSegment(sketch, "E46.3.22.0", {"start": v(-58.84, -51.97) * mm, "end": v(-67.76, -60) * mm});
            skLineSegment(sketch, "E46.6.22.0", {"start": v(-57.84, -53.08) * mm, "end": v(-66.75, -61.11) * mm});
            skLineSegment(sketch, "E46.9.22.0", {"start": v(-57.84, -53.08) * mm, "end": v(-58.84, -51.97) * mm});
            skLineSegment(sketch, "E46.1.23.0", {"start": v(-60, -67.76) * mm, "end": v(-61.11, -66.75) * mm});
            skLineSegment(sketch, "E46.3.23.0", {"start": v(-53.08, -57.84) * mm, "end": v(-61.11, -66.75) * mm});
            skLineSegment(sketch, "E46.6.23.0", {"start": v(-51.97, -58.84) * mm, "end": v(-60, -67.76) * mm});
            skLineSegment(sketch, "E46.9.23.0", {"start": v(-51.97, -58.84) * mm, "end": v(-53.08, -57.84) * mm});
            skLineSegment(sketch, "E46.1.24.0", {"start": v(-52.59, -73.66) * mm, "end": v(-53.8, -72.78) * mm});
            skLineSegment(sketch, "E46.3.24.0", {"start": v(-46.75, -63.07) * mm, "end": v(-53.8, -72.78) * mm});
            skLineSegment(sketch, "E46.6.24.0", {"start": v(-45.53, -63.95) * mm, "end": v(-52.59, -73.66) * mm});
            skLineSegment(sketch, "E46.9.24.0", {"start": v(-45.53, -63.95) * mm, "end": v(-46.75, -63.07) * mm});
            skLineSegment(sketch, "E46.1.25.0", {"start": v(-44.6, -78.75) * mm, "end": v(-45.9, -78) * mm});
            skLineSegment(sketch, "E46.3.25.0", {"start": v(-39.9, -67.6) * mm, "end": v(-45.9, -78) * mm});
            skLineSegment(sketch, "E46.6.25.0", {"start": v(-38.6, -68.36) * mm, "end": v(-44.6, -78.75) * mm});
            skLineSegment(sketch, "E46.9.25.0", {"start": v(-38.6, -68.36) * mm, "end": v(-39.9, -67.6) * mm});
            skLineSegment(sketch, "E46.1.26.0", {"start": v(-36.12, -82.98) * mm, "end": v(-37.5, -82.37) * mm});
            skLineSegment(sketch, "E46.3.26.0", {"start": v(-32.61, -71.4) * mm, "end": v(-37.5, -82.37) * mm});
            skLineSegment(sketch, "E46.6.26.0", {"start": v(-31.24, -72.02) * mm, "end": v(-36.12, -82.98) * mm});
            skLineSegment(sketch, "E46.9.26.0", {"start": v(-31.24, -72.02) * mm, "end": v(-32.61, -71.4) * mm});
            skLineSegment(sketch, "E46.1.27.0", {"start": v(-27.25, -86.3) * mm, "end": v(-28.68, -85.84) * mm});
            skLineSegment(sketch, "E46.3.27.0", {"start": v(-24.97, -74.43) * mm, "end": v(-28.68, -85.84) * mm});
            skLineSegment(sketch, "E46.6.27.0", {"start": v(-23.54, -74.89) * mm, "end": v(-27.25, -86.3) * mm});
            skLineSegment(sketch, "E46.9.27.0", {"start": v(-23.54, -74.89) * mm, "end": v(-24.97, -74.43) * mm});
            skLineSegment(sketch, "E46.1.28.0", {"start": v(-18.08, -88.68) * mm, "end": v(-19.55, -88.37) * mm});
            skLineSegment(sketch, "E46.3.28.0", {"start": v(-17.05, -76.63) * mm, "end": v(-19.55, -88.37) * mm});
            skLineSegment(sketch, "E46.6.28.0", {"start": v(-15.59, -76.94) * mm, "end": v(-18.08, -88.68) * mm});
            skLineSegment(sketch, "E46.9.28.0", {"start": v(-15.59, -76.94) * mm, "end": v(-17.05, -76.63) * mm});
            skLineSegment(sketch, "E46.1.29.0", {"start": v(-8.71, -90.08) * mm, "end": v(-10.2, -89.93) * mm});
            skLineSegment(sketch, "E46.3.29.0", {"start": v(-8.95, -78) * mm, "end": v(-10.2, -89.93) * mm});
            skLineSegment(sketch, "E46.6.29.0", {"start": v(-7.46, -78.15) * mm, "end": v(-8.71, -90.08) * mm});
            skLineSegment(sketch, "E46.9.29.0", {"start": v(-7.46, -78.15) * mm, "end": v(-8.95, -78) * mm});
            skLineSegment(sketch, "E46.1.30.0", {"start": v(0.75, -90.5) * mm, "end": v(-0.75, -90.5) * mm});
            skLineSegment(sketch, "E46.3.30.0", {"start": v(-0.75, -78.5) * mm, "end": v(-0.75, -90.5) * mm});
            skLineSegment(sketch, "E46.6.30.0", {"start": v(0.75, -78.5) * mm, "end": v(0.75, -90.5) * mm});
            skLineSegment(sketch, "E46.9.30.0", {"start": v(0.75, -78.5) * mm, "end": v(-0.75, -78.5) * mm});
            skLineSegment(sketch, "E46.1.31.0", {"start": v(10.2, -89.93) * mm, "end": v(8.71, -90.08) * mm});
            skLineSegment(sketch, "E46.3.31.0", {"start": v(7.46, -78.15) * mm, "end": v(8.71, -90.08) * mm});
            skLineSegment(sketch, "E46.6.31.0", {"start": v(8.95, -78) * mm, "end": v(10.2, -89.93) * mm});
            skLineSegment(sketch, "E46.9.31.0", {"start": v(8.95, -78) * mm, "end": v(7.46, -78.15) * mm});
            skLineSegment(sketch, "E46.1.32.0", {"start": v(19.55, -88.37) * mm, "end": v(18.08, -88.68) * mm});
            skLineSegment(sketch, "E46.3.32.0", {"start": v(15.59, -76.94) * mm, "end": v(18.08, -88.68) * mm});
            skLineSegment(sketch, "E46.6.32.0", {"start": v(17.05, -76.63) * mm, "end": v(19.55, -88.37) * mm});
            skLineSegment(sketch, "E46.9.32.0", {"start": v(17.05, -76.63) * mm, "end": v(15.59, -76.94) * mm});
            skLineSegment(sketch, "E46.1.33.0", {"start": v(28.68, -85.84) * mm, "end": v(27.25, -86.3) * mm});
            skLineSegment(sketch, "E46.3.33.0", {"start": v(23.54, -74.89) * mm, "end": v(27.25, -86.3) * mm});
            skLineSegment(sketch, "E46.6.33.0", {"start": v(24.97, -74.43) * mm, "end": v(28.68, -85.84) * mm});
            skLineSegment(sketch, "E46.9.33.0", {"start": v(24.97, -74.43) * mm, "end": v(23.54, -74.89) * mm});
            skLineSegment(sketch, "E46.1.34.0", {"start": v(37.5, -82.37) * mm, "end": v(36.12, -82.98) * mm});
            skLineSegment(sketch, "E46.3.34.0", {"start": v(31.24, -72.02) * mm, "end": v(36.12, -82.98) * mm});
            skLineSegment(sketch, "E46.6.34.0", {"start": v(32.61, -71.4) * mm, "end": v(37.5, -82.37) * mm});
            skLineSegment(sketch, "E46.9.34.0", {"start": v(32.61, -71.4) * mm, "end": v(31.24, -72.02) * mm});
            skLineSegment(sketch, "E46.1.35.0", {"start": v(45.9, -78) * mm, "end": v(44.6, -78.75) * mm});
            skLineSegment(sketch, "E46.3.35.0", {"start": v(38.6, -68.36) * mm, "end": v(44.6, -78.75) * mm});
            skLineSegment(sketch, "E46.6.35.0", {"start": v(39.9, -67.6) * mm, "end": v(45.9, -78) * mm});
            skLineSegment(sketch, "E46.9.35.0", {"start": v(39.9, -67.6) * mm, "end": v(38.6, -68.36) * mm});
            skLineSegment(sketch, "E46.1.36.0", {"start": v(53.8, -72.78) * mm, "end": v(52.59, -73.66) * mm});
            skLineSegment(sketch, "E46.3.36.0", {"start": v(45.53, -63.95) * mm, "end": v(52.59, -73.66) * mm});
            skLineSegment(sketch, "E46.6.36.0", {"start": v(46.75, -63.07) * mm, "end": v(53.8, -72.78) * mm});
            skLineSegment(sketch, "E46.9.36.0", {"start": v(46.75, -63.07) * mm, "end": v(45.53, -63.95) * mm});
            skLineSegment(sketch, "E46.1.37.0", {"start": v(61.11, -66.75) * mm, "end": v(60, -67.76) * mm});
            skLineSegment(sketch, "E46.3.37.0", {"start": v(51.97, -58.84) * mm, "end": v(60, -67.76) * mm});
            skLineSegment(sketch, "E46.6.37.0", {"start": v(53.08, -57.84) * mm, "end": v(61.11, -66.75) * mm});
            skLineSegment(sketch, "E46.9.37.0", {"start": v(53.08, -57.84) * mm, "end": v(51.97, -58.84) * mm});
            skLineSegment(sketch, "E46.1.38.0", {"start": v(67.76, -60) * mm, "end": v(66.75, -61.11) * mm});
            skLineSegment(sketch, "E46.3.38.0", {"start": v(57.84, -53.08) * mm, "end": v(66.75, -61.11) * mm});
            skLineSegment(sketch, "E46.6.38.0", {"start": v(58.84, -51.97) * mm, "end": v(67.76, -60) * mm});
            skLineSegment(sketch, "E46.9.38.0", {"start": v(58.84, -51.97) * mm, "end": v(57.84, -53.08) * mm});
            skLineSegment(sketch, "E46.1.39.0", {"start": v(73.66, -52.59) * mm, "end": v(72.78, -53.8) * mm});
            skLineSegment(sketch, "E46.3.39.0", {"start": v(63.07, -46.75) * mm, "end": v(72.78, -53.8) * mm});
            skLineSegment(sketch, "E46.6.39.0", {"start": v(63.95, -45.53) * mm, "end": v(73.66, -52.59) * mm});
            skLineSegment(sketch, "E46.9.39.0", {"start": v(63.95, -45.53) * mm, "end": v(63.07, -46.75) * mm});
            skLineSegment(sketch, "E46.1.40.0", {"start": v(78.75, -44.6) * mm, "end": v(78, -45.9) * mm});
            skLineSegment(sketch, "E46.3.40.0", {"start": v(67.6, -39.9) * mm, "end": v(78, -45.9) * mm});
            skLineSegment(sketch, "E46.6.40.0", {"start": v(68.36, -38.6) * mm, "end": v(78.75, -44.6) * mm});
            skLineSegment(sketch, "E46.9.40.0", {"start": v(68.36, -38.6) * mm, "end": v(67.6, -39.9) * mm});
            skLineSegment(sketch, "E46.1.41.0", {"start": v(82.98, -36.12) * mm, "end": v(82.37, -37.5) * mm});
            skLineSegment(sketch, "E46.3.41.0", {"start": v(71.4, -32.61) * mm, "end": v(82.37, -37.5) * mm});
            skLineSegment(sketch, "E46.6.41.0", {"start": v(72.02, -31.24) * mm, "end": v(82.98, -36.12) * mm});
            skLineSegment(sketch, "E46.9.41.0", {"start": v(72.02, -31.24) * mm, "end": v(71.4, -32.61) * mm});
            skLineSegment(sketch, "E46.1.42.0", {"start": v(86.3, -27.25) * mm, "end": v(85.84, -28.68) * mm});
            skLineSegment(sketch, "E46.3.42.0", {"start": v(74.43, -24.97) * mm, "end": v(85.84, -28.68) * mm});
            skLineSegment(sketch, "E46.6.42.0", {"start": v(74.89, -23.54) * mm, "end": v(86.3, -27.25) * mm});
            skLineSegment(sketch, "E46.9.42.0", {"start": v(74.89, -23.54) * mm, "end": v(74.43, -24.97) * mm});
            skLineSegment(sketch, "E46.1.43.0", {"start": v(88.68, -18.08) * mm, "end": v(88.37, -19.55) * mm});
            skLineSegment(sketch, "E46.3.43.0", {"start": v(76.63, -17.05) * mm, "end": v(88.37, -19.55) * mm});
            skLineSegment(sketch, "E46.6.43.0", {"start": v(76.94, -15.59) * mm, "end": v(88.68, -18.08) * mm});
            skLineSegment(sketch, "E46.9.43.0", {"start": v(76.94, -15.59) * mm, "end": v(76.63, -17.05) * mm});
            skLineSegment(sketch, "E46.1.44.0", {"start": v(90.08, -8.71) * mm, "end": v(89.93, -10.2) * mm});
            skLineSegment(sketch, "E46.3.44.0", {"start": v(78, -8.95) * mm, "end": v(89.93, -10.2) * mm});
            skLineSegment(sketch, "E46.6.44.0", {"start": v(78.15, -7.46) * mm, "end": v(90.08, -8.71) * mm});
            skLineSegment(sketch, "E46.9.44.0", {"start": v(78.15, -7.46) * mm, "end": v(78, -8.95) * mm});
            skLineSegment(sketch, "E46.1.45.0", {"start": v(90.5, 0.75) * mm, "end": v(90.5, -0.75) * mm});
            skLineSegment(sketch, "E46.3.45.0", {"start": v(78.5, -0.75) * mm, "end": v(90.5, -0.75) * mm});
            skLineSegment(sketch, "E46.6.45.0", {"start": v(78.5, 0.75) * mm, "end": v(90.5, 0.75) * mm});
            skLineSegment(sketch, "E46.9.45.0", {"start": v(78.5, 0.75) * mm, "end": v(78.5, -0.75) * mm});
            skLineSegment(sketch, "E46.1.46.0", {"start": v(89.93, 10.2) * mm, "end": v(90.08, 8.71) * mm});
            skLineSegment(sketch, "E46.3.46.0", {"start": v(78.15, 7.46) * mm, "end": v(90.08, 8.71) * mm});
            skLineSegment(sketch, "E46.6.46.0", {"start": v(78, 8.95) * mm, "end": v(89.93, 10.2) * mm});
            skLineSegment(sketch, "E46.9.46.0", {"start": v(78, 8.95) * mm, "end": v(78.15, 7.46) * mm});
            skLineSegment(sketch, "E46.1.47.0", {"start": v(88.37, 19.55) * mm, "end": v(88.68, 18.08) * mm});
            skLineSegment(sketch, "E46.3.47.0", {"start": v(76.94, 15.59) * mm, "end": v(88.68, 18.08) * mm});
            skLineSegment(sketch, "E46.6.47.0", {"start": v(76.63, 17.05) * mm, "end": v(88.37, 19.55) * mm});
            skLineSegment(sketch, "E46.9.47.0", {"start": v(76.63, 17.05) * mm, "end": v(76.94, 15.59) * mm});
            skLineSegment(sketch, "E46.1.48.0", {"start": v(85.84, 28.68) * mm, "end": v(86.3, 27.25) * mm});
            skLineSegment(sketch, "E46.3.48.0", {"start": v(74.89, 23.54) * mm, "end": v(86.3, 27.25) * mm});
            skLineSegment(sketch, "E46.6.48.0", {"start": v(74.43, 24.97) * mm, "end": v(85.84, 28.68) * mm});
            skLineSegment(sketch, "E46.9.48.0", {"start": v(74.43, 24.97) * mm, "end": v(74.89, 23.54) * mm});
            skLineSegment(sketch, "E46.1.49.0", {"start": v(82.37, 37.5) * mm, "end": v(82.98, 36.12) * mm});
            skLineSegment(sketch, "E46.3.49.0", {"start": v(72.02, 31.24) * mm, "end": v(82.98, 36.12) * mm});
            skLineSegment(sketch, "E46.6.49.0", {"start": v(71.4, 32.61) * mm, "end": v(82.37, 37.5) * mm});
            skLineSegment(sketch, "E46.9.49.0", {"start": v(71.4, 32.61) * mm, "end": v(72.02, 31.24) * mm});
            skLineSegment(sketch, "E46.1.50.0", {"start": v(78, 45.9) * mm, "end": v(78.75, 44.6) * mm});
            skLineSegment(sketch, "E46.3.50.0", {"start": v(68.36, 38.6) * mm, "end": v(78.75, 44.6) * mm});
            skLineSegment(sketch, "E46.6.50.0", {"start": v(67.6, 39.9) * mm, "end": v(78, 45.9) * mm});
            skLineSegment(sketch, "E46.9.50.0", {"start": v(67.6, 39.9) * mm, "end": v(68.36, 38.6) * mm});
            skLineSegment(sketch, "E46.1.51.0", {"start": v(72.78, 53.8) * mm, "end": v(73.66, 52.59) * mm});
            skLineSegment(sketch, "E46.3.51.0", {"start": v(63.95, 45.53) * mm, "end": v(73.66, 52.59) * mm});
            skLineSegment(sketch, "E46.6.51.0", {"start": v(63.07, 46.75) * mm, "end": v(72.78, 53.8) * mm});
            skLineSegment(sketch, "E46.9.51.0", {"start": v(63.07, 46.75) * mm, "end": v(63.95, 45.53) * mm});
            skLineSegment(sketch, "E46.1.52.0", {"start": v(66.75, 61.11) * mm, "end": v(67.76, 60) * mm});
            skLineSegment(sketch, "E46.3.52.0", {"start": v(58.84, 51.97) * mm, "end": v(67.76, 60) * mm});
            skLineSegment(sketch, "E46.6.52.0", {"start": v(57.84, 53.08) * mm, "end": v(66.75, 61.11) * mm});
            skLineSegment(sketch, "E46.9.52.0", {"start": v(57.84, 53.08) * mm, "end": v(58.84, 51.97) * mm});
            skLineSegment(sketch, "E46.1.53.0", {"start": v(60, 67.76) * mm, "end": v(61.11, 66.75) * mm});
            skLineSegment(sketch, "E46.3.53.0", {"start": v(53.08, 57.84) * mm, "end": v(61.11, 66.75) * mm});
            skLineSegment(sketch, "E46.6.53.0", {"start": v(51.97, 58.84) * mm, "end": v(60, 67.76) * mm});
            skLineSegment(sketch, "E46.9.53.0", {"start": v(51.97, 58.84) * mm, "end": v(53.08, 57.84) * mm});
            skLineSegment(sketch, "E46.1.54.0", {"start": v(52.59, 73.66) * mm, "end": v(53.8, 72.78) * mm});
            skLineSegment(sketch, "E46.3.54.0", {"start": v(46.75, 63.07) * mm, "end": v(53.8, 72.78) * mm});
            skLineSegment(sketch, "E46.6.54.0", {"start": v(45.53, 63.95) * mm, "end": v(52.59, 73.66) * mm});
            skLineSegment(sketch, "E46.9.54.0", {"start": v(45.53, 63.95) * mm, "end": v(46.75, 63.07) * mm});
            skLineSegment(sketch, "E46.1.55.0", {"start": v(44.6, 78.75) * mm, "end": v(45.9, 78) * mm});
            skLineSegment(sketch, "E46.3.55.0", {"start": v(39.9, 67.6) * mm, "end": v(45.9, 78) * mm});
            skLineSegment(sketch, "E46.6.55.0", {"start": v(38.6, 68.36) * mm, "end": v(44.6, 78.75) * mm});
            skLineSegment(sketch, "E46.9.55.0", {"start": v(38.6, 68.36) * mm, "end": v(39.9, 67.6) * mm});
            skLineSegment(sketch, "E46.1.56.0", {"start": v(36.12, 82.98) * mm, "end": v(37.5, 82.37) * mm});
            skLineSegment(sketch, "E46.3.56.0", {"start": v(32.61, 71.4) * mm, "end": v(37.5, 82.37) * mm});
            skLineSegment(sketch, "E46.6.56.0", {"start": v(31.24, 72.02) * mm, "end": v(36.12, 82.98) * mm});
            skLineSegment(sketch, "E46.9.56.0", {"start": v(31.24, 72.02) * mm, "end": v(32.61, 71.4) * mm});
            skLineSegment(sketch, "E46.1.57.0", {"start": v(27.25, 86.3) * mm, "end": v(28.68, 85.84) * mm});
            skLineSegment(sketch, "E46.3.57.0", {"start": v(24.97, 74.43) * mm, "end": v(28.68, 85.84) * mm});
            skLineSegment(sketch, "E46.6.57.0", {"start": v(23.54, 74.89) * mm, "end": v(27.25, 86.3) * mm});
            skLineSegment(sketch, "E46.9.57.0", {"start": v(23.54, 74.89) * mm, "end": v(24.97, 74.43) * mm});
            skLineSegment(sketch, "E46.1.58.0", {"start": v(18.08, 88.68) * mm, "end": v(19.55, 88.37) * mm});
            skLineSegment(sketch, "E46.3.58.0", {"start": v(17.05, 76.63) * mm, "end": v(19.55, 88.37) * mm});
            skLineSegment(sketch, "E46.6.58.0", {"start": v(15.59, 76.94) * mm, "end": v(18.08, 88.68) * mm});
            skLineSegment(sketch, "E46.9.58.0", {"start": v(15.59, 76.94) * mm, "end": v(17.05, 76.63) * mm});
            skLineSegment(sketch, "E46.1.59.0", {"start": v(8.71, 90.08) * mm, "end": v(10.2, 89.93) * mm});
            skLineSegment(sketch, "E46.3.59.0", {"start": v(8.95, 78) * mm, "end": v(10.2, 89.93) * mm});
            skLineSegment(sketch, "E46.6.59.0", {"start": v(7.46, 78.15) * mm, "end": v(8.71, 90.08) * mm});
            skLineSegment(sketch, "E46.9.59.0", {"start": v(7.46, 78.15) * mm, "end": v(8.95, 78) * mm});
            skSolve(sketch);
        }
        {
            var Q0;
            Q0 = qSketchRegion(id + "F27", true);
            extrude(context, id + "F28", {"entities" : qUnion([Q0]), "operationType" : NewBodyOperationType.REMOVE, "oppositeDirection" : true, "depth" : 0.2 * mm, "offsetDistance" : 25 * mm});
        }
        {
            var Q0;
            Q0=makeQuery(id+"F26.boolean.opBoolean","COPY",FACE,{"derivedFrom":makeQuery(id+"F26.opExtrude","CAP_FACE",FACE,{"disambiguationData":[OSD([sQuery(id+"F25.wireOp",EDGE,"E41.bottom"),sQuery(id+"F25.wireOp",EDGE,"E41.top"),sQuery(id+"F25.wireOp",EDGE,"E41.left"),sQuery(id+"F25.wireOp",EDGE,"E41.right")])],"isStart":false})});
            extrude(context, id + "F29", {"entities" : qUnion([Q0]), "depth" : 1 * mm, "offsetDistance" : 25 * mm});
        }
        {
            var Q0;
            Q0=makeQuery(id+"F28.boolean.opBoolean","COPY",FACE,{"derivedFrom":makeQuery(id+"F28.opExtrude","CAP_FACE",FACE,{"disambiguationData":[OSD([sQuery(id+"F27.wireOp",EDGE,"E46.1.59.0"),sQuery(id+"F27.wireOp",EDGE,"E46.3.59.0"),sQuery(id+"F27.wireOp",EDGE,"E46.6.59.0"),sQuery(id+"F27.wireOp",EDGE,"E46.9.59.0")])],"isStart":false})});
            extrude(context, id + "F30", {"entities" : qUnion([Q0]), "depth" : 0.4 * mm, "offsetDistance" : 25 * mm});
        }
        {
            var Q0;
            Q0=makeQuery(id+"F15.opExtrude","CAP_FACE",FACE,{"disambiguationData":[OSD([sQuery(id+"F14.wireOp",EDGE,"E21.0"),sQuery(id+"F14.wireOp",EDGE,"E22"),sQuery(id+"F14.wireOp",EDGE,"E23"),sQuery(id+"F14.wireOp",EDGE,"E24"),sQuery(id+"F14.wireOp",EDGE,"E25.MirrorCS"),sQuery(id+"F14.wireOp",EDGE,"E26.MirrorCS"),sQuery(id+"F14.wireOp",EDGE,"E27.1.0"),sQuery(id+"F14.wireOp",EDGE,"E27.1.1"),sQuery(id+"F14.wireOp",EDGE,"E27.1.2"),sQuery(id+"F14.wireOp",EDGE,"E27.1.3"),sQuery(id+"F14.wireOp",EDGE,"E27.2.0"),sQuery(id+"F14.wireOp",EDGE,"E27.2.1"),sQuery(id+"F14.wireOp",EDGE,"E27.2.2"),sQuery(id+"F14.wireOp",EDGE,"E27.2.3"),sQuery(id+"F14.wireOp",EDGE,"E28.1.3.0"),sQuery(id+"F14.wireOp",EDGE,"E28.3.3.0"),sQuery(id+"F14.wireOp",EDGE,"E28.6.3.0"),sQuery(id+"F14.wireOp",EDGE,"E28.9.3.0"),sQuery(id+"F14.wireOp",EDGE,"E28.1.4.0"),sQuery(id+"F14.wireOp",EDGE,"E28.3.4.0"),sQuery(id+"F14.wireOp",EDGE,"E28.6.4.0"),sQuery(id+"F14.wireOp",EDGE,"E28.9.4.0"),sQuery(id+"F14.wireOp",EDGE,"E28.1.5.0"),sQuery(id+"F14.wireOp",EDGE,"E28.3.5.0"),sQuery(id+"F14.wireOp",EDGE,"E28.6.5.0"),sQuery(id+"F14.wireOp",EDGE,"E28.9.5.0"),sQuery(id+"F14.wireOp",EDGE,"E28.1.6.0"),sQuery(id+"F14.wireOp",EDGE,"E28.3.6.0"),sQuery(id+"F14.wireOp",EDGE,"E28.6.6.0"),sQuery(id+"F14.wireOp",EDGE,"E28.9.6.0"),sQuery(id+"F14.wireOp",EDGE,"E28.1.7.0"),sQuery(id+"F14.wireOp",EDGE,"E28.3.7.0"),sQuery(id+"F14.wireOp",EDGE,"E28.6.7.0"),sQuery(id+"F14.wireOp",EDGE,"E28.9.7.0"),sQuery(id+"F14.wireOp",EDGE,"E28.1.8.0"),sQuery(id+"F14.wireOp",EDGE,"E28.3.8.0"),sQuery(id+"F14.wireOp",EDGE,"E28.6.8.0"),sQuery(id+"F14.wireOp",EDGE,"E28.9.8.0"),sQuery(id+"F14.wireOp",EDGE,"E28.1.9.0"),sQuery(id+"F14.wireOp",EDGE,"E28.3.9.0"),sQuery(id+"F14.wireOp",EDGE,"E28.6.9.0"),sQuery(id+"F14.wireOp",EDGE,"E28.9.9.0"),sQuery(id+"F14.wireOp",EDGE,"E28.1.10.0"),sQuery(id+"F14.wireOp",EDGE,"E28.3.10.0"),sQuery(id+"F14.wireOp",EDGE,"E28.6.10.0"),sQuery(id+"F14.wireOp",EDGE,"E28.9.10.0"),sQuery(id+"F14.wireOp",EDGE,"E28.1.11.0"),sQuery(id+"F14.wireOp",EDGE,"E28.3.11.0"),sQuery(id+"F14.wireOp",EDGE,"E28.6.11.0"),sQuery(id+"F14.wireOp",EDGE,"E28.9.11.0"),sQuery(id+"F14.wireOp",EDGE,"E28.1.12.0"),sQuery(id+"F14.wireOp",EDGE,"E28.3.12.0"),sQuery(id+"F14.wireOp",EDGE,"E28.6.12.0"),sQuery(id+"F14.wireOp",EDGE,"E28.9.12.0"),sQuery(id+"F14.wireOp",EDGE,"E28.1.13.0"),sQuery(id+"F14.wireOp",EDGE,"E28.3.13.0"),sQuery(id+"F14.wireOp",EDGE,"E28.6.13.0"),sQuery(id+"F14.wireOp",EDGE,"E28.9.13.0"),sQuery(id+"F14.wireOp",EDGE,"E28.1.14.0"),sQuery(id+"F14.wireOp",EDGE,"E28.3.14.0"),sQuery(id+"F14.wireOp",EDGE,"E28.6.14.0"),sQuery(id+"F14.wireOp",EDGE,"E28.9.14.0"),sQuery(id+"F14.wireOp",EDGE,"E28.1.15.0"),sQuery(id+"F14.wireOp",EDGE,"E28.3.15.0"),sQuery(id+"F14.wireOp",EDGE,"E28.6.15.0"),sQuery(id+"F14.wireOp",EDGE,"E28.9.15.0"),sQuery(id+"F14.wireOp",EDGE,"E28.1.16.0"),sQuery(id+"F14.wireOp",EDGE,"E28.3.16.0"),sQuery(id+"F14.wireOp",EDGE,"E28.6.16.0"),sQuery(id+"F14.wireOp",EDGE,"E28.9.16.0"),sQuery(id+"F14.wireOp",EDGE,"E28.1.17.0"),sQuery(id+"F14.wireOp",EDGE,"E28.3.17.0"),sQuery(id+"F14.wireOp",EDGE,"E28.6.17.0"),sQuery(id+"F14.wireOp",EDGE,"E28.9.17.0"),sQuery(id+"F14.wireOp",EDGE,"E28.1.18.0"),sQuery(id+"F14.wireOp",EDGE,"E28.3.18.0"),sQuery(id+"F14.wireOp",EDGE,"E28.6.18.0"),sQuery(id+"F14.wireOp",EDGE,"E28.9.18.0"),sQuery(id+"F14.wireOp",EDGE,"E28.1.19.0"),sQuery(id+"F14.wireOp",EDGE,"E28.3.19.0"),sQuery(id+"F14.wireOp",EDGE,"E28.6.19.0"),sQuery(id+"F14.wireOp",EDGE,"E28.9.19.0"),sQuery(id+"F14.wireOp",EDGE,"E28.1.20.0"),sQuery(id+"F14.wireOp",EDGE,"E28.3.20.0"),sQuery(id+"F14.wireOp",EDGE,"E28.6.20.0"),sQuery(id+"F14.wireOp",EDGE,"E28.9.20.0"),sQuery(id+"F14.wireOp",EDGE,"E28.1.21.0"),sQuery(id+"F14.wireOp",EDGE,"E28.3.21.0"),sQuery(id+"F14.wireOp",EDGE,"E28.6.21.0"),sQuery(id+"F14.wireOp",EDGE,"E28.9.21.0"),sQuery(id+"F14.wireOp",EDGE,"E28.1.22.0"),sQuery(id+"F14.wireOp",EDGE,"E28.3.22.0"),sQuery(id+"F14.wireOp",EDGE,"E28.6.22.0"),sQuery(id+"F14.wireOp",EDGE,"E28.9.22.0"),sQuery(id+"F14.wireOp",EDGE,"E28.1.23.0"),sQuery(id+"F14.wireOp",EDGE,"E28.3.23.0"),sQuery(id+"F14.wireOp",EDGE,"E28.6.23.0"),sQuery(id+"F14.wireOp",EDGE,"E28.9.23.0"),sQuery(id+"F14.wireOp",EDGE,"E28.1.24.0"),sQuery(id+"F14.wireOp",EDGE,"E28.3.24.0"),sQuery(id+"F14.wireOp",EDGE,"E28.6.24.0"),sQuery(id+"F14.wireOp",EDGE,"E28.9.24.0"),sQuery(id+"F14.wireOp",EDGE,"E28.1.25.0"),sQuery(id+"F14.wireOp",EDGE,"E28.3.25.0"),sQuery(id+"F14.wireOp",EDGE,"E28.6.25.0"),sQuery(id+"F14.wireOp",EDGE,"E28.9.25.0"),sQuery(id+"F14.wireOp",EDGE,"E28.1.26.0"),sQuery(id+"F14.wireOp",EDGE,"E28.3.26.0"),sQuery(id+"F14.wireOp",EDGE,"E28.6.26.0"),sQuery(id+"F14.wireOp",EDGE,"E28.9.26.0"),sQuery(id+"F14.wireOp",EDGE,"E28.1.27.0"),sQuery(id+"F14.wireOp",EDGE,"E28.3.27.0"),sQuery(id+"F14.wireOp",EDGE,"E28.6.27.0"),sQuery(id+"F14.wireOp",EDGE,"E28.9.27.0"),sQuery(id+"F14.wireOp",EDGE,"E28.1.28.0"),sQuery(id+"F14.wireOp",EDGE,"E28.3.28.0"),sQuery(id+"F14.wireOp",EDGE,"E28.6.28.0"),sQuery(id+"F14.wireOp",EDGE,"E28.9.28.0"),sQuery(id+"F14.wireOp",EDGE,"E28.1.29.0"),sQuery(id+"F14.wireOp",EDGE,"E28.3.29.0"),sQuery(id+"F14.wireOp",EDGE,"E28.6.29.0"),sQuery(id+"F14.wireOp",EDGE,"E28.9.29.0"),sQuery(id+"F14.wireOp",EDGE,"E28.1.30.0"),sQuery(id+"F14.wireOp",EDGE,"E28.3.30.0"),sQuery(id+"F14.wireOp",EDGE,"E28.6.30.0"),sQuery(id+"F14.wireOp",EDGE,"E28.9.30.0"),sQuery(id+"F14.wireOp",EDGE,"E28.1.31.0"),sQuery(id+"F14.wireOp",EDGE,"E28.3.31.0"),sQuery(id+"F14.wireOp",EDGE,"E28.6.31.0"),sQuery(id+"F14.wireOp",EDGE,"E28.9.31.0"),sQuery(id+"F14.wireOp",EDGE,"E28.1.32.0"),sQuery(id+"F14.wireOp",EDGE,"E28.3.32.0"),sQuery(id+"F14.wireOp",EDGE,"E28.6.32.0"),sQuery(id+"F14.wireOp",EDGE,"E28.9.32.0"),sQuery(id+"F14.wireOp",EDGE,"E28.1.33.0"),sQuery(id+"F14.wireOp",EDGE,"E28.3.33.0"),sQuery(id+"F14.wireOp",EDGE,"E28.6.33.0"),sQuery(id+"F14.wireOp",EDGE,"E28.9.33.0"),sQuery(id+"F14.wireOp",EDGE,"E28.1.34.0"),sQuery(id+"F14.wireOp",EDGE,"E28.3.34.0"),sQuery(id+"F14.wireOp",EDGE,"E28.6.34.0"),sQuery(id+"F14.wireOp",EDGE,"E28.9.34.0"),sQuery(id+"F14.wireOp",EDGE,"E28.1.35.0"),sQuery(id+"F14.wireOp",EDGE,"E28.3.35.0"),sQuery(id+"F14.wireOp",EDGE,"E28.6.35.0"),sQuery(id+"F14.wireOp",EDGE,"E28.9.35.0"),sQuery(id+"F14.wireOp",EDGE,"E28.1.36.0"),sQuery(id+"F14.wireOp",EDGE,"E28.3.36.0"),sQuery(id+"F14.wireOp",EDGE,"E28.6.36.0"),sQuery(id+"F14.wireOp",EDGE,"E28.9.36.0"),sQuery(id+"F14.wireOp",EDGE,"E28.1.37.0"),sQuery(id+"F14.wireOp",EDGE,"E28.3.37.0"),sQuery(id+"F14.wireOp",EDGE,"E28.6.37.0"),sQuery(id+"F14.wireOp",EDGE,"E28.9.37.0"),sQuery(id+"F14.wireOp",EDGE,"E28.1.38.0"),sQuery(id+"F14.wireOp",EDGE,"E28.3.38.0"),sQuery(id+"F14.wireOp",EDGE,"E28.6.38.0"),sQuery(id+"F14.wireOp",EDGE,"E28.9.38.0"),sQuery(id+"F14.wireOp",EDGE,"E28.1.39.0"),sQuery(id+"F14.wireOp",EDGE,"E28.3.39.0"),sQuery(id+"F14.wireOp",EDGE,"E28.6.39.0"),sQuery(id+"F14.wireOp",EDGE,"E28.9.39.0")])],"isStart":false});
            var sketch = newSketch(context, id + "F31", { "sketchPlane" : qUnion([Q0])});
            skCircle(sketch, "E47.0", {"center": v(0, 0) * mm, "radius": 3 * mm});
            skCircle(sketch, "E48.0", {"center": v(0, 0) * mm, "radius": 5 * mm});
            skSolve(sketch);
        }
        {
            var Q0;
            Q0 = qSketchRegion(id + "F31", true);
            extrude(context, id + "F32", {"entities" : qUnion([Q0]), "operationType" : NewBodyOperationType.ADD, "depth" : 5 * mm, "offsetDistance" : 25 * mm});
        }
        {
            var Q0;
            Q0=makeQuery(id+"F32.opExtrude","CAP_FACE",FACE,{"disambiguationData":[OSD([sQuery(id+"F31.wireOp",EDGE,"E47.0"),sQuery(id+"F31.wireOp",EDGE,"E48.0")])],"isStart":false});
            var sketch = newSketch(context, id + "F33", { "sketchPlane" : qUnion([Q0])});
            skCircle(sketch, "E49.0.0", {"center": v(0, 0) * mm, "radius": 3 * mm});
            skCircle(sketch, "E50.0", {"center": v(0, 0) * mm, "radius": 5 * mm});
            skLineSegment(sketch, "E51", {"start": v(3, 4) * mm, "end": v(1.5, 53.98) * mm});
            skLineSegment(sketch, "E52", {"start": v(1.5, 53.98) * mm, "end": v(0, 53.98) * mm});
            skLineSegment(sketch, "E53.MirrorCS", {"start": v(-3, 4) * mm, "end": v(-1.5, 53.98) * mm});
            skLineSegment(sketch, "E54.MirrorCS", {"start": v(-1.5, 53.98) * mm, "end": v(0, 53.98) * mm});
            skSolve(sketch);
        }
        {
            var Q0;
            Q0 = qSketchRegion(id + "F33", true);
            extrude(context, id + "F34", {"entities" : qUnion([Q0]), "operationType" : NewBodyOperationType.ADD, "depth" : 1 * mm, "offsetDistance" : 25 * mm});
        }
        {
            var Q0;
            Q0=makeQuery(id+"F6.opExtrude","CAP_FACE",FACE,{"disambiguationData":[OSD([sQuery(id+"F0.wireOp",EDGE,"E0")])],"isStart":false});
            var sketch = newSketch(context, id + "F35", { "sketchPlane" : qUnion([Q0])});
            skCircle(sketch, "E55", {"center": v(0, 0) * mm, "radius": 5 * mm});
            skLineSegment(sketch, "E56", {"start": v(2, 4.58) * mm, "end": v(0.5, 80) * mm});
            skLineSegment(sketch, "E57", {"start": v(0.5, 80) * mm, "end": v(0, 80) * mm});
            skLineSegment(sketch, "E58.MirrorCS", {"start": v(-2, 4.58) * mm, "end": v(-0.5, 80) * mm});
            skLineSegment(sketch, "E59.MirrorCS", {"start": v(-0.5, 80) * mm, "end": v(0, 80) * mm});
            skSolve(sketch);
        }
        {
            var Q0;
            Q0 = qSketchRegion(id + "F35", true);
            extrude(context, id + "F36", {"entities" : qUnion([Q0]), "operationType" : NewBodyOperationType.ADD, "oppositeDirection" : true, "depth" : 1 * mm, "offsetDistance" : 25 * mm});
        }
    });
